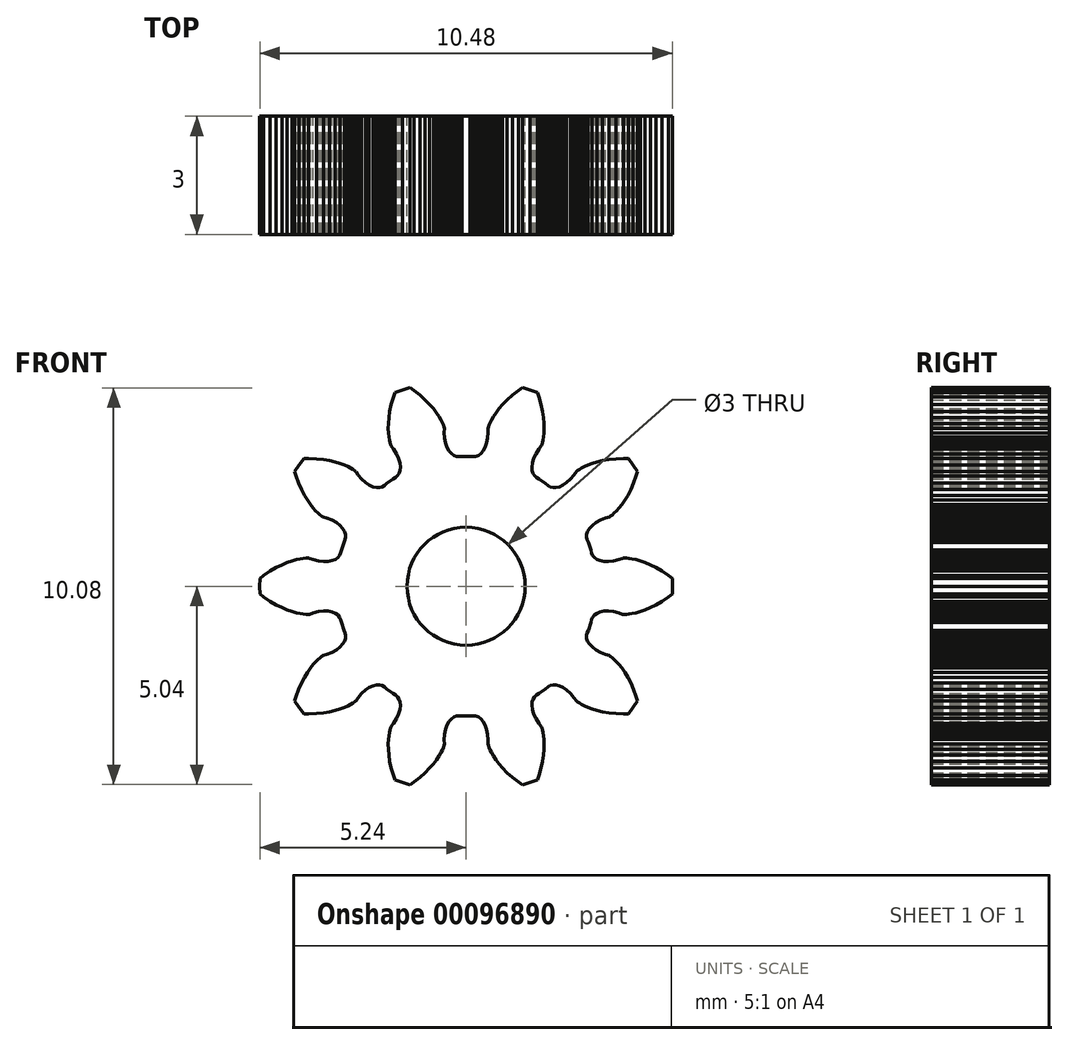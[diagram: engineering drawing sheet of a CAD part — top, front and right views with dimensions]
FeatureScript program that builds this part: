
annotation { "Feature Type Name" : "Feature", "Feature Type Description" : "" }
export const myFeature = defineFeature(function(context is Context, id is Id, definition is map)
    precondition{}
    {
        {
            var Q0;
            Q0=qCreatedBy(makeId("Front.planeOp"),FACE);
            var sketch = newSketch(context, id + "F0", { "sketchPlane" : qUnion([Q0])});
            skCircle(sketch, "E0", {"center": v(0, 0) * mm, "radius": 1.5 * mm});
            skSolve(sketch);
        }
        {
            var Q0;
            Q0=qCreatedBy(makeId("Front.planeOp"),FACE);
            var sketch = newSketch(context, id + "F1", { "sketchPlane" : qUnion([Q0])});
            skLineSegment(sketch, "E1", {"start": v(4.12, -3.24) * mm, "end": v(4.24, -3.08) * mm});
            skLineSegment(sketch, "E2", {"start": v(4.24, -3.08) * mm, "end": v(4.36, -2.92) * mm});
            skLineSegment(sketch, "E3", {"start": v(4.36, -2.92) * mm, "end": v(4.32, -2.8) * mm});
            skLineSegment(sketch, "E4", {"start": v(4.32, -2.8) * mm, "end": v(4.25, -2.62) * mm});
            skLineSegment(sketch, "E5", {"start": v(4.25, -2.62) * mm, "end": v(4.18, -2.46) * mm});
            skLineSegment(sketch, "E6", {"start": v(4.18, -2.46) * mm, "end": v(4.1, -2.31) * mm});
            skLineSegment(sketch, "E7", {"start": v(4.1, -2.31) * mm, "end": v(4.03, -2.19) * mm});
            skLineSegment(sketch, "E8", {"start": v(4.03, -2.19) * mm, "end": v(3.96, -2.08) * mm});
            skLineSegment(sketch, "E9", {"start": v(3.96, -2.08) * mm, "end": v(3.89, -2) * mm});
            skLineSegment(sketch, "E10", {"start": v(3.89, -2) * mm, "end": v(3.82, -1.92) * mm});
            skLineSegment(sketch, "E11", {"start": v(3.82, -1.92) * mm, "end": v(3.76, -1.86) * mm});
            skLineSegment(sketch, "E12", {"start": v(3.76, -1.86) * mm, "end": v(3.71, -1.82) * mm});
            skLineSegment(sketch, "E13", {"start": v(3.71, -1.82) * mm, "end": v(3.67, -1.79) * mm});
            skLineSegment(sketch, "E14", {"start": v(3.67, -1.79) * mm, "end": v(3.64, -1.77) * mm});
            skLineSegment(sketch, "E15", {"start": v(3.64, -1.77) * mm, "end": v(3.64, -1.76) * mm});
            skLineSegment(sketch, "E16", {"start": v(3.64, -1.76) * mm, "end": v(3.54, -1.74) * mm});
            skLineSegment(sketch, "E17", {"start": v(3.54, -1.74) * mm, "end": v(3.4, -1.68) * mm});
            skLineSegment(sketch, "E18", {"start": v(3.4, -1.68) * mm, "end": v(3.3, -1.62) * mm});
            skLineSegment(sketch, "E19", {"start": v(3.3, -1.62) * mm, "end": v(3.2, -1.55) * mm});
            skLineSegment(sketch, "E20", {"start": v(3.2, -1.55) * mm, "end": v(3.14, -1.47) * mm});
            skLineSegment(sketch, "E21", {"start": v(3.14, -1.47) * mm, "end": v(3.09, -1.4) * mm});
            skLineSegment(sketch, "E22", {"start": v(3.09, -1.4) * mm, "end": v(3.06, -1.32) * mm});
            skLineSegment(sketch, "E23", {"start": v(3.06, -1.32) * mm, "end": v(3.06, -1.25) * mm});
            skLineSegment(sketch, "E24", {"start": v(3.06, -1.25) * mm, "end": v(3.08, -1.18) * mm});
            skLineSegment(sketch, "E25", {"start": v(3.08, -1.18) * mm, "end": v(3.1, -1.12) * mm});
            skLineSegment(sketch, "E26", {"start": v(3.1, -1.12) * mm, "end": v(3.17, -0.92) * mm});
            skLineSegment(sketch, "E27", {"start": v(3.17, -0.92) * mm, "end": v(3.18, -0.85) * mm});
            skLineSegment(sketch, "E28", {"start": v(3.18, -0.85) * mm, "end": v(3.2, -0.79) * mm});
            skLineSegment(sketch, "E29", {"start": v(3.2, -0.79) * mm, "end": v(3.26, -0.73) * mm});
            skLineSegment(sketch, "E30", {"start": v(3.26, -0.73) * mm, "end": v(3.32, -0.69) * mm});
            skLineSegment(sketch, "E31", {"start": v(3.32, -0.69) * mm, "end": v(3.4, -0.65) * mm});
            skLineSegment(sketch, "E32", {"start": v(3.4, -0.65) * mm, "end": v(3.5, -0.63) * mm});
            skLineSegment(sketch, "E33", {"start": v(3.5, -0.63) * mm, "end": v(3.62, -0.63) * mm});
            skLineSegment(sketch, "E34", {"start": v(3.62, -0.63) * mm, "end": v(3.75, -0.64) * mm});
            skLineSegment(sketch, "E35", {"start": v(3.75, -0.64) * mm, "end": v(3.89, -0.68) * mm});
            skLineSegment(sketch, "E36", {"start": v(3.89, -0.68) * mm, "end": v(3.98, -0.71) * mm});
            skLineSegment(sketch, "E37", {"start": v(3.98, -0.71) * mm, "end": v(3.99, -0.71) * mm});
            skLineSegment(sketch, "E38", {"start": v(3.99, -0.71) * mm, "end": v(4.02, -0.71) * mm});
            skLineSegment(sketch, "E39", {"start": v(4.02, -0.71) * mm, "end": v(4.07, -0.71) * mm});
            skLineSegment(sketch, "E40", {"start": v(4.07, -0.71) * mm, "end": v(4.14, -0.7) * mm});
            skLineSegment(sketch, "E41", {"start": v(4.14, -0.7) * mm, "end": v(4.22, -0.7) * mm});
            skLineSegment(sketch, "E42", {"start": v(4.22, -0.7) * mm, "end": v(4.31, -0.67) * mm});
            skLineSegment(sketch, "E43", {"start": v(4.31, -0.67) * mm, "end": v(4.42, -0.64) * mm});
            skLineSegment(sketch, "E44", {"start": v(4.42, -0.64) * mm, "end": v(4.55, -0.6) * mm});
            skLineSegment(sketch, "E45", {"start": v(4.55, -0.6) * mm, "end": v(4.68, -0.54) * mm});
            skLineSegment(sketch, "E46", {"start": v(4.68, -0.54) * mm, "end": v(4.83, -0.47) * mm});
            skLineSegment(sketch, "E47", {"start": v(4.83, -0.47) * mm, "end": v(4.98, -0.38) * mm});
            skLineSegment(sketch, "E48", {"start": v(4.98, -0.38) * mm, "end": v(5.14, -0.27) * mm});
            skLineSegment(sketch, "E49", {"start": v(5.14, -0.27) * mm, "end": v(5.24, -0.2) * mm});
            skLineSegment(sketch, "E50", {"start": v(5.24, -0.2) * mm, "end": v(5.24, 0) * mm});
            skLineSegment(sketch, "E51", {"start": v(5.24, 0) * mm, "end": v(5.24, 0.2) * mm});
            skLineSegment(sketch, "E52", {"start": v(5.24, 0.2) * mm, "end": v(5.14, 0.27) * mm});
            skLineSegment(sketch, "E53", {"start": v(5.14, 0.27) * mm, "end": v(4.98, 0.38) * mm});
            skLineSegment(sketch, "E54", {"start": v(4.98, 0.38) * mm, "end": v(4.83, 0.47) * mm});
            skLineSegment(sketch, "E55", {"start": v(4.83, 0.47) * mm, "end": v(4.68, 0.54) * mm});
            skLineSegment(sketch, "E56", {"start": v(4.68, 0.54) * mm, "end": v(4.55, 0.6) * mm});
            skLineSegment(sketch, "E57", {"start": v(4.55, 0.6) * mm, "end": v(4.42, 0.64) * mm});
            skLineSegment(sketch, "E58", {"start": v(4.42, 0.64) * mm, "end": v(4.31, 0.67) * mm});
            skLineSegment(sketch, "E59", {"start": v(4.31, 0.67) * mm, "end": v(4.22, 0.7) * mm});
            skLineSegment(sketch, "E60", {"start": v(4.22, 0.7) * mm, "end": v(4.14, 0.7) * mm});
            skLineSegment(sketch, "E61", {"start": v(4.14, 0.7) * mm, "end": v(4.07, 0.71) * mm});
            skLineSegment(sketch, "E62", {"start": v(4.07, 0.71) * mm, "end": v(4.02, 0.71) * mm});
            skLineSegment(sketch, "E63", {"start": v(4.02, 0.71) * mm, "end": v(3.99, 0.71) * mm});
            skLineSegment(sketch, "E64", {"start": v(3.99, 0.71) * mm, "end": v(3.98, 0.71) * mm});
            skLineSegment(sketch, "E65", {"start": v(3.98, 0.71) * mm, "end": v(3.89, 0.68) * mm});
            skLineSegment(sketch, "E66", {"start": v(3.89, 0.68) * mm, "end": v(3.75, 0.64) * mm});
            skLineSegment(sketch, "E67", {"start": v(3.75, 0.64) * mm, "end": v(3.62, 0.63) * mm});
            skLineSegment(sketch, "E68", {"start": v(3.62, 0.63) * mm, "end": v(3.5, 0.63) * mm});
            skLineSegment(sketch, "E69", {"start": v(3.5, 0.63) * mm, "end": v(3.4, 0.65) * mm});
            skLineSegment(sketch, "E70", {"start": v(3.4, 0.65) * mm, "end": v(3.32, 0.69) * mm});
            skLineSegment(sketch, "E71", {"start": v(3.32, 0.69) * mm, "end": v(3.26, 0.73) * mm});
            skLineSegment(sketch, "E72", {"start": v(3.26, 0.73) * mm, "end": v(3.2, 0.79) * mm});
            skLineSegment(sketch, "E73", {"start": v(3.2, 0.79) * mm, "end": v(3.18, 0.85) * mm});
            skLineSegment(sketch, "E74", {"start": v(3.18, 0.85) * mm, "end": v(3.17, 0.92) * mm});
            skLineSegment(sketch, "E75", {"start": v(3.17, 0.92) * mm, "end": v(3.1, 1.12) * mm});
            skLineSegment(sketch, "E76", {"start": v(3.1, 1.12) * mm, "end": v(3.08, 1.18) * mm});
            skLineSegment(sketch, "E77", {"start": v(3.08, 1.18) * mm, "end": v(3.06, 1.25) * mm});
            skLineSegment(sketch, "E78", {"start": v(3.06, 1.25) * mm, "end": v(3.06, 1.32) * mm});
            skLineSegment(sketch, "E79", {"start": v(3.06, 1.32) * mm, "end": v(3.09, 1.4) * mm});
            skLineSegment(sketch, "E80", {"start": v(3.09, 1.4) * mm, "end": v(3.14, 1.47) * mm});
            skLineSegment(sketch, "E81", {"start": v(3.14, 1.47) * mm, "end": v(3.2, 1.55) * mm});
            skLineSegment(sketch, "E82", {"start": v(3.2, 1.55) * mm, "end": v(3.3, 1.62) * mm});
            skLineSegment(sketch, "E83", {"start": v(3.3, 1.62) * mm, "end": v(3.4, 1.68) * mm});
            skLineSegment(sketch, "E84", {"start": v(3.4, 1.68) * mm, "end": v(3.54, 1.74) * mm});
            skLineSegment(sketch, "E85", {"start": v(3.54, 1.74) * mm, "end": v(3.64, 1.76) * mm});
            skLineSegment(sketch, "E86", {"start": v(3.64, 1.76) * mm, "end": v(3.64, 1.77) * mm});
            skLineSegment(sketch, "E87", {"start": v(3.64, 1.77) * mm, "end": v(3.67, 1.79) * mm});
            skLineSegment(sketch, "E88", {"start": v(3.67, 1.79) * mm, "end": v(3.71, 1.82) * mm});
            skLineSegment(sketch, "E89", {"start": v(3.71, 1.82) * mm, "end": v(3.76, 1.86) * mm});
            skLineSegment(sketch, "E90", {"start": v(3.76, 1.86) * mm, "end": v(3.82, 1.92) * mm});
            skLineSegment(sketch, "E91", {"start": v(3.82, 1.92) * mm, "end": v(3.89, 2) * mm});
            skLineSegment(sketch, "E92", {"start": v(3.89, 2) * mm, "end": v(3.96, 2.08) * mm});
            skLineSegment(sketch, "E93", {"start": v(3.96, 2.08) * mm, "end": v(4.03, 2.19) * mm});
            skLineSegment(sketch, "E94", {"start": v(4.03, 2.19) * mm, "end": v(4.1, 2.31) * mm});
            skLineSegment(sketch, "E95", {"start": v(4.1, 2.31) * mm, "end": v(4.18, 2.46) * mm});
            skLineSegment(sketch, "E96", {"start": v(4.18, 2.46) * mm, "end": v(4.25, 2.62) * mm});
            skLineSegment(sketch, "E97", {"start": v(4.25, 2.62) * mm, "end": v(4.32, 2.8) * mm});
            skLineSegment(sketch, "E98", {"start": v(4.32, 2.8) * mm, "end": v(4.36, 2.92) * mm});
            skLineSegment(sketch, "E99", {"start": v(4.36, 2.92) * mm, "end": v(4.24, 3.08) * mm});
            skLineSegment(sketch, "E100", {"start": v(4.24, 3.08) * mm, "end": v(4.12, 3.24) * mm});
            skLineSegment(sketch, "E101", {"start": v(4.12, 3.24) * mm, "end": v(4, 3.24) * mm});
            skLineSegment(sketch, "E102", {"start": v(4, 3.24) * mm, "end": v(3.8, 3.24) * mm});
            skLineSegment(sketch, "E103", {"start": v(3.8, 3.24) * mm, "end": v(3.63, 3.22) * mm});
            skLineSegment(sketch, "E104", {"start": v(3.63, 3.22) * mm, "end": v(3.47, 3.2) * mm});
            skLineSegment(sketch, "E105", {"start": v(3.47, 3.2) * mm, "end": v(3.33, 3.16) * mm});
            skLineSegment(sketch, "E106", {"start": v(3.33, 3.16) * mm, "end": v(3.2, 3.12) * mm});
            skLineSegment(sketch, "E107", {"start": v(3.2, 3.12) * mm, "end": v(3.1, 3.08) * mm});
            skLineSegment(sketch, "E108", {"start": v(3.1, 3.08) * mm, "end": v(3, 3.04) * mm});
            skLineSegment(sketch, "E109", {"start": v(3, 3.04) * mm, "end": v(2.93, 3) * mm});
            skLineSegment(sketch, "E110", {"start": v(2.93, 3) * mm, "end": v(2.87, 2.97) * mm});
            skLineSegment(sketch, "E111", {"start": v(2.87, 2.97) * mm, "end": v(2.83, 2.94) * mm});
            skLineSegment(sketch, "E112", {"start": v(2.83, 2.94) * mm, "end": v(2.8, 2.92) * mm});
            skLineSegment(sketch, "E113", {"start": v(2.8, 2.92) * mm, "end": v(2.8, 2.91) * mm});
            skLineSegment(sketch, "E114", {"start": v(2.8, 2.91) * mm, "end": v(2.74, 2.83) * mm});
            skLineSegment(sketch, "E115", {"start": v(2.74, 2.83) * mm, "end": v(2.65, 2.72) * mm});
            skLineSegment(sketch, "E116", {"start": v(2.65, 2.72) * mm, "end": v(2.56, 2.64) * mm});
            skLineSegment(sketch, "E117", {"start": v(2.56, 2.64) * mm, "end": v(2.46, 2.57) * mm});
            skLineSegment(sketch, "E118", {"start": v(2.46, 2.57) * mm, "end": v(2.37, 2.53) * mm});
            skLineSegment(sketch, "E119", {"start": v(2.37, 2.53) * mm, "end": v(2.28, 2.5) * mm});
            skLineSegment(sketch, "E120", {"start": v(2.28, 2.5) * mm, "end": v(2.2, 2.5) * mm});
            skLineSegment(sketch, "E121", {"start": v(2.2, 2.5) * mm, "end": v(2.13, 2.52) * mm});
            skLineSegment(sketch, "E122", {"start": v(2.13, 2.52) * mm, "end": v(2.08, 2.56) * mm});
            skLineSegment(sketch, "E123", {"start": v(2.08, 2.56) * mm, "end": v(2.02, 2.6) * mm});
            skLineSegment(sketch, "E124", {"start": v(2.02, 2.6) * mm, "end": v(1.85, 2.73) * mm});
            skLineSegment(sketch, "E125", {"start": v(1.85, 2.73) * mm, "end": v(1.8, 2.77) * mm});
            skLineSegment(sketch, "E126", {"start": v(1.8, 2.77) * mm, "end": v(1.74, 2.8) * mm});
            skLineSegment(sketch, "E127", {"start": v(1.74, 2.8) * mm, "end": v(1.7, 2.87) * mm});
            skLineSegment(sketch, "E128", {"start": v(1.7, 2.87) * mm, "end": v(1.68, 2.95) * mm});
            skLineSegment(sketch, "E129", {"start": v(1.68, 2.95) * mm, "end": v(1.67, 3.03) * mm});
            skLineSegment(sketch, "E130", {"start": v(1.67, 3.03) * mm, "end": v(1.68, 3.13) * mm});
            skLineSegment(sketch, "E131", {"start": v(1.68, 3.13) * mm, "end": v(1.72, 3.25) * mm});
            skLineSegment(sketch, "E132", {"start": v(1.72, 3.25) * mm, "end": v(1.77, 3.36) * mm});
            skLineSegment(sketch, "E133", {"start": v(1.77, 3.36) * mm, "end": v(1.85, 3.49) * mm});
            skLineSegment(sketch, "E134", {"start": v(1.85, 3.49) * mm, "end": v(1.9, 3.56) * mm});
            skLineSegment(sketch, "E135", {"start": v(1.9, 3.56) * mm, "end": v(1.9, 3.57) * mm});
            skLineSegment(sketch, "E136", {"start": v(1.9, 3.57) * mm, "end": v(1.92, 3.6) * mm});
            skLineSegment(sketch, "E137", {"start": v(1.92, 3.6) * mm, "end": v(1.94, 3.65) * mm});
            skLineSegment(sketch, "E138", {"start": v(1.94, 3.65) * mm, "end": v(1.95, 3.72) * mm});
            skLineSegment(sketch, "E139", {"start": v(1.95, 3.72) * mm, "end": v(1.96, 3.8) * mm});
            skLineSegment(sketch, "E140", {"start": v(1.96, 3.8) * mm, "end": v(1.97, 3.9) * mm});
            skLineSegment(sketch, "E141", {"start": v(1.97, 3.9) * mm, "end": v(1.98, 4) * mm});
            skLineSegment(sketch, "E142", {"start": v(1.98, 4) * mm, "end": v(1.98, 4.14) * mm});
            skLineSegment(sketch, "E143", {"start": v(1.98, 4.14) * mm, "end": v(1.96, 4.28) * mm});
            skLineSegment(sketch, "E144", {"start": v(1.96, 4.28) * mm, "end": v(1.94, 4.44) * mm});
            skLineSegment(sketch, "E145", {"start": v(1.94, 4.44) * mm, "end": v(1.9, 4.62) * mm});
            skLineSegment(sketch, "E146", {"start": v(1.9, 4.62) * mm, "end": v(1.85, 4.8) * mm});
            skLineSegment(sketch, "E147", {"start": v(1.85, 4.8) * mm, "end": v(1.81, 4.92) * mm});
            skLineSegment(sketch, "E148", {"start": v(1.81, 4.92) * mm, "end": v(1.62, 4.99) * mm});
            skLineSegment(sketch, "E149", {"start": v(1.62, 4.99) * mm, "end": v(1.43, 5.04) * mm});
            skLineSegment(sketch, "E150", {"start": v(1.43, 5.04) * mm, "end": v(1.33, 4.97) * mm});
            skLineSegment(sketch, "E151", {"start": v(1.33, 4.97) * mm, "end": v(1.18, 4.85) * mm});
            skLineSegment(sketch, "E152", {"start": v(1.18, 4.85) * mm, "end": v(1.04, 4.74) * mm});
            skLineSegment(sketch, "E153", {"start": v(1.04, 4.74) * mm, "end": v(0.93, 4.62) * mm});
            skLineSegment(sketch, "E154", {"start": v(0.93, 4.62) * mm, "end": v(0.83, 4.51) * mm});
            skLineSegment(sketch, "E155", {"start": v(0.83, 4.51) * mm, "end": v(0.76, 4.4) * mm});
            skLineSegment(sketch, "E156", {"start": v(0.76, 4.4) * mm, "end": v(0.7, 4.31) * mm});
            skLineSegment(sketch, "E157", {"start": v(0.7, 4.31) * mm, "end": v(0.64, 4.23) * mm});
            skLineSegment(sketch, "E158", {"start": v(0.64, 4.23) * mm, "end": v(0.6, 4.15) * mm});
            skLineSegment(sketch, "E159", {"start": v(0.6, 4.15) * mm, "end": v(0.58, 4.1) * mm});
            skLineSegment(sketch, "E160", {"start": v(0.58, 4.1) * mm, "end": v(0.56, 4.04) * mm});
            skLineSegment(sketch, "E161", {"start": v(0.56, 4.04) * mm, "end": v(0.55, 4.01) * mm});
            skLineSegment(sketch, "E162", {"start": v(0.55, 4.01) * mm, "end": v(0.55, 4) * mm});
            skLineSegment(sketch, "E163", {"start": v(0.55, 4) * mm, "end": v(0.56, 3.9) * mm});
            skLineSegment(sketch, "E164", {"start": v(0.56, 3.9) * mm, "end": v(0.54, 3.76) * mm});
            skLineSegment(sketch, "E165", {"start": v(0.54, 3.76) * mm, "end": v(0.52, 3.63) * mm});
            skLineSegment(sketch, "E166", {"start": v(0.52, 3.63) * mm, "end": v(0.48, 3.53) * mm});
            skLineSegment(sketch, "E167", {"start": v(0.48, 3.53) * mm, "end": v(0.43, 3.44) * mm});
            skLineSegment(sketch, "E168", {"start": v(0.43, 3.44) * mm, "end": v(0.37, 3.37) * mm});
            skLineSegment(sketch, "E169", {"start": v(0.37, 3.37) * mm, "end": v(0.31, 3.32) * mm});
            skLineSegment(sketch, "E170", {"start": v(0.31, 3.32) * mm, "end": v(0.24, 3.3) * mm});
            skLineSegment(sketch, "E171", {"start": v(0.24, 3.3) * mm, "end": v(0.18, 3.3) * mm});
            skLineSegment(sketch, "E172", {"start": v(0.18, 3.3) * mm, "end": v(0.1, 3.3) * mm});
            skLineSegment(sketch, "E173", {"start": v(0.1, 3.3) * mm, "end": v(-0.1, 3.3) * mm});
            skLineSegment(sketch, "E174", {"start": v(-0.1, 3.3) * mm, "end": v(-0.18, 3.3) * mm});
            skLineSegment(sketch, "E175", {"start": v(-0.18, 3.3) * mm, "end": v(-0.24, 3.3) * mm});
            skLineSegment(sketch, "E176", {"start": v(-0.24, 3.3) * mm, "end": v(-0.31, 3.32) * mm});
            skLineSegment(sketch, "E177", {"start": v(-0.31, 3.32) * mm, "end": v(-0.37, 3.37) * mm});
            skLineSegment(sketch, "E178", {"start": v(-0.37, 3.37) * mm, "end": v(-0.43, 3.44) * mm});
            skLineSegment(sketch, "E179", {"start": v(-0.43, 3.44) * mm, "end": v(-0.48, 3.53) * mm});
            skLineSegment(sketch, "E180", {"start": v(-0.48, 3.53) * mm, "end": v(-0.52, 3.63) * mm});
            skLineSegment(sketch, "E181", {"start": v(-0.52, 3.63) * mm, "end": v(-0.54, 3.76) * mm});
            skLineSegment(sketch, "E182", {"start": v(-0.54, 3.76) * mm, "end": v(-0.56, 3.9) * mm});
            skLineSegment(sketch, "E183", {"start": v(-0.56, 3.9) * mm, "end": v(-0.55, 4) * mm});
            skLineSegment(sketch, "E184", {"start": v(-0.55, 4) * mm, "end": v(-0.55, 4.01) * mm});
            skLineSegment(sketch, "E185", {"start": v(-0.55, 4.01) * mm, "end": v(-0.56, 4.04) * mm});
            skLineSegment(sketch, "E186", {"start": v(-0.56, 4.04) * mm, "end": v(-0.58, 4.1) * mm});
            skLineSegment(sketch, "E187", {"start": v(-0.58, 4.1) * mm, "end": v(-0.6, 4.15) * mm});
            skLineSegment(sketch, "E188", {"start": v(-0.6, 4.15) * mm, "end": v(-0.64, 4.23) * mm});
            skLineSegment(sketch, "E189", {"start": v(-0.64, 4.23) * mm, "end": v(-0.7, 4.31) * mm});
            skLineSegment(sketch, "E190", {"start": v(-0.7, 4.31) * mm, "end": v(-0.76, 4.4) * mm});
            skLineSegment(sketch, "E191", {"start": v(-0.76, 4.4) * mm, "end": v(-0.83, 4.51) * mm});
            skLineSegment(sketch, "E192", {"start": v(-0.83, 4.51) * mm, "end": v(-0.93, 4.62) * mm});
            skLineSegment(sketch, "E193", {"start": v(-0.93, 4.62) * mm, "end": v(-1.04, 4.74) * mm});
            skLineSegment(sketch, "E194", {"start": v(-1.04, 4.74) * mm, "end": v(-1.18, 4.85) * mm});
            skLineSegment(sketch, "E195", {"start": v(-1.18, 4.85) * mm, "end": v(-1.33, 4.97) * mm});
            skLineSegment(sketch, "E196", {"start": v(-1.33, 4.97) * mm, "end": v(-1.43, 5.04) * mm});
            skLineSegment(sketch, "E197", {"start": v(-1.43, 5.04) * mm, "end": v(-1.62, 4.99) * mm});
            skLineSegment(sketch, "E198", {"start": v(-1.62, 4.99) * mm, "end": v(-1.81, 4.92) * mm});
            skLineSegment(sketch, "E199", {"start": v(-1.81, 4.92) * mm, "end": v(-1.85, 4.8) * mm});
            skLineSegment(sketch, "E200", {"start": v(-1.85, 4.8) * mm, "end": v(-1.9, 4.62) * mm});
            skLineSegment(sketch, "E201", {"start": v(-1.9, 4.62) * mm, "end": v(-1.94, 4.44) * mm});
            skLineSegment(sketch, "E202", {"start": v(-1.94, 4.44) * mm, "end": v(-1.96, 4.28) * mm});
            skLineSegment(sketch, "E203", {"start": v(-1.96, 4.28) * mm, "end": v(-1.98, 4.14) * mm});
            skLineSegment(sketch, "E204", {"start": v(-1.98, 4.14) * mm, "end": v(-1.98, 4) * mm});
            skLineSegment(sketch, "E205", {"start": v(-1.98, 4) * mm, "end": v(-1.97, 3.9) * mm});
            skLineSegment(sketch, "E206", {"start": v(-1.97, 3.9) * mm, "end": v(-1.96, 3.8) * mm});
            skLineSegment(sketch, "E207", {"start": v(-1.96, 3.8) * mm, "end": v(-1.95, 3.72) * mm});
            skLineSegment(sketch, "E208", {"start": v(-1.95, 3.72) * mm, "end": v(-1.94, 3.65) * mm});
            skLineSegment(sketch, "E209", {"start": v(-1.94, 3.65) * mm, "end": v(-1.92, 3.6) * mm});
            skLineSegment(sketch, "E210", {"start": v(-1.92, 3.6) * mm, "end": v(-1.9, 3.57) * mm});
            skLineSegment(sketch, "E211", {"start": v(-1.9, 3.57) * mm, "end": v(-1.9, 3.56) * mm});
            skLineSegment(sketch, "E212", {"start": v(-1.9, 3.56) * mm, "end": v(-1.85, 3.49) * mm});
            skLineSegment(sketch, "E213", {"start": v(-1.85, 3.49) * mm, "end": v(-1.77, 3.36) * mm});
            skLineSegment(sketch, "E214", {"start": v(-1.77, 3.36) * mm, "end": v(-1.72, 3.25) * mm});
            skLineSegment(sketch, "E215", {"start": v(-1.72, 3.25) * mm, "end": v(-1.68, 3.13) * mm});
            skLineSegment(sketch, "E216", {"start": v(-1.68, 3.13) * mm, "end": v(-1.67, 3.03) * mm});
            skLineSegment(sketch, "E217", {"start": v(-1.67, 3.03) * mm, "end": v(-1.68, 2.95) * mm});
            skLineSegment(sketch, "E218", {"start": v(-1.68, 2.95) * mm, "end": v(-1.7, 2.87) * mm});
            skLineSegment(sketch, "E219", {"start": v(-1.7, 2.87) * mm, "end": v(-1.74, 2.8) * mm});
            skLineSegment(sketch, "E220", {"start": v(-1.74, 2.8) * mm, "end": v(-1.8, 2.77) * mm});
            skLineSegment(sketch, "E221", {"start": v(-1.8, 2.77) * mm, "end": v(-1.85, 2.73) * mm});
            skLineSegment(sketch, "E222", {"start": v(-1.85, 2.73) * mm, "end": v(-2.02, 2.6) * mm});
            skLineSegment(sketch, "E223", {"start": v(-2.02, 2.6) * mm, "end": v(-2.08, 2.56) * mm});
            skLineSegment(sketch, "E224", {"start": v(-2.08, 2.56) * mm, "end": v(-2.13, 2.52) * mm});
            skLineSegment(sketch, "E225", {"start": v(-2.13, 2.52) * mm, "end": v(-2.2, 2.5) * mm});
            skLineSegment(sketch, "E226", {"start": v(-2.2, 2.5) * mm, "end": v(-2.28, 2.5) * mm});
            skLineSegment(sketch, "E227", {"start": v(-2.28, 2.5) * mm, "end": v(-2.37, 2.53) * mm});
            skLineSegment(sketch, "E228", {"start": v(-2.37, 2.53) * mm, "end": v(-2.46, 2.57) * mm});
            skLineSegment(sketch, "E229", {"start": v(-2.46, 2.57) * mm, "end": v(-2.56, 2.64) * mm});
            skLineSegment(sketch, "E230", {"start": v(-2.56, 2.64) * mm, "end": v(-2.65, 2.72) * mm});
            skLineSegment(sketch, "E231", {"start": v(-2.65, 2.72) * mm, "end": v(-2.74, 2.83) * mm});
            skLineSegment(sketch, "E232", {"start": v(-2.74, 2.83) * mm, "end": v(-2.8, 2.91) * mm});
            skLineSegment(sketch, "E233", {"start": v(-2.8, 2.91) * mm, "end": v(-2.8, 2.92) * mm});
            skLineSegment(sketch, "E234", {"start": v(-2.8, 2.92) * mm, "end": v(-2.83, 2.94) * mm});
            skLineSegment(sketch, "E235", {"start": v(-2.83, 2.94) * mm, "end": v(-2.87, 2.97) * mm});
            skLineSegment(sketch, "E236", {"start": v(-2.87, 2.97) * mm, "end": v(-2.93, 3) * mm});
            skLineSegment(sketch, "E237", {"start": v(-2.93, 3) * mm, "end": v(-3, 3.04) * mm});
            skLineSegment(sketch, "E238", {"start": v(-3, 3.04) * mm, "end": v(-3.1, 3.08) * mm});
            skLineSegment(sketch, "E239", {"start": v(-3.1, 3.08) * mm, "end": v(-3.2, 3.12) * mm});
            skLineSegment(sketch, "E240", {"start": v(-3.2, 3.12) * mm, "end": v(-3.33, 3.16) * mm});
            skLineSegment(sketch, "E241", {"start": v(-3.33, 3.16) * mm, "end": v(-3.47, 3.2) * mm});
            skLineSegment(sketch, "E242", {"start": v(-3.47, 3.2) * mm, "end": v(-3.63, 3.22) * mm});
            skLineSegment(sketch, "E243", {"start": v(-3.63, 3.22) * mm, "end": v(-3.8, 3.24) * mm});
            skLineSegment(sketch, "E244", {"start": v(-3.8, 3.24) * mm, "end": v(-4, 3.24) * mm});
            skLineSegment(sketch, "E245", {"start": v(-4, 3.24) * mm, "end": v(-4.12, 3.24) * mm});
            skLineSegment(sketch, "E246", {"start": v(-4.12, 3.24) * mm, "end": v(-4.24, 3.08) * mm});
            skLineSegment(sketch, "E247", {"start": v(-4.24, 3.08) * mm, "end": v(-4.36, 2.92) * mm});
            skLineSegment(sketch, "E248", {"start": v(-4.36, 2.92) * mm, "end": v(-4.32, 2.8) * mm});
            skLineSegment(sketch, "E249", {"start": v(-4.32, 2.8) * mm, "end": v(-4.25, 2.62) * mm});
            skLineSegment(sketch, "E250", {"start": v(-4.25, 2.62) * mm, "end": v(-4.18, 2.46) * mm});
            skLineSegment(sketch, "E251", {"start": v(-4.18, 2.46) * mm, "end": v(-4.1, 2.31) * mm});
            skLineSegment(sketch, "E252", {"start": v(-4.1, 2.31) * mm, "end": v(-4.03, 2.19) * mm});
            skLineSegment(sketch, "E253", {"start": v(-4.03, 2.19) * mm, "end": v(-3.96, 2.08) * mm});
            skLineSegment(sketch, "E254", {"start": v(-3.96, 2.08) * mm, "end": v(-3.89, 2) * mm});
            skLineSegment(sketch, "E255", {"start": v(-3.89, 2) * mm, "end": v(-3.82, 1.92) * mm});
            skLineSegment(sketch, "E256", {"start": v(-3.82, 1.92) * mm, "end": v(-3.76, 1.86) * mm});
            skLineSegment(sketch, "E257", {"start": v(-3.76, 1.86) * mm, "end": v(-3.71, 1.82) * mm});
            skLineSegment(sketch, "E258", {"start": v(-3.71, 1.82) * mm, "end": v(-3.67, 1.79) * mm});
            skLineSegment(sketch, "E259", {"start": v(-3.67, 1.79) * mm, "end": v(-3.64, 1.77) * mm});
            skLineSegment(sketch, "E260", {"start": v(-3.64, 1.77) * mm, "end": v(-3.64, 1.76) * mm});
            skLineSegment(sketch, "E261", {"start": v(-3.64, 1.76) * mm, "end": v(-3.54, 1.74) * mm});
            skLineSegment(sketch, "E262", {"start": v(-3.54, 1.74) * mm, "end": v(-3.4, 1.68) * mm});
            skLineSegment(sketch, "E263", {"start": v(-3.4, 1.68) * mm, "end": v(-3.3, 1.62) * mm});
            skLineSegment(sketch, "E264", {"start": v(-3.3, 1.62) * mm, "end": v(-3.2, 1.55) * mm});
            skLineSegment(sketch, "E265", {"start": v(-3.2, 1.55) * mm, "end": v(-3.14, 1.47) * mm});
            skLineSegment(sketch, "E266", {"start": v(-3.14, 1.47) * mm, "end": v(-3.09, 1.4) * mm});
            skLineSegment(sketch, "E267", {"start": v(-3.09, 1.4) * mm, "end": v(-3.06, 1.32) * mm});
            skLineSegment(sketch, "E268", {"start": v(-3.06, 1.32) * mm, "end": v(-3.06, 1.25) * mm});
            skLineSegment(sketch, "E269", {"start": v(-3.06, 1.25) * mm, "end": v(-3.08, 1.18) * mm});
            skLineSegment(sketch, "E270", {"start": v(-3.08, 1.18) * mm, "end": v(-3.1, 1.12) * mm});
            skLineSegment(sketch, "E271", {"start": v(-3.1, 1.12) * mm, "end": v(-3.17, 0.92) * mm});
            skLineSegment(sketch, "E272", {"start": v(-3.17, 0.92) * mm, "end": v(-3.18, 0.85) * mm});
            skLineSegment(sketch, "E273", {"start": v(-3.18, 0.85) * mm, "end": v(-3.2, 0.79) * mm});
            skLineSegment(sketch, "E274", {"start": v(-3.2, 0.79) * mm, "end": v(-3.26, 0.73) * mm});
            skLineSegment(sketch, "E275", {"start": v(-3.26, 0.73) * mm, "end": v(-3.32, 0.69) * mm});
            skLineSegment(sketch, "E276", {"start": v(-3.32, 0.69) * mm, "end": v(-3.4, 0.65) * mm});
            skLineSegment(sketch, "E277", {"start": v(-3.4, 0.65) * mm, "end": v(-3.5, 0.63) * mm});
            skLineSegment(sketch, "E278", {"start": v(-3.5, 0.63) * mm, "end": v(-3.62, 0.63) * mm});
            skLineSegment(sketch, "E279", {"start": v(-3.62, 0.63) * mm, "end": v(-3.75, 0.64) * mm});
            skLineSegment(sketch, "E280", {"start": v(-3.75, 0.64) * mm, "end": v(-3.89, 0.68) * mm});
            skLineSegment(sketch, "E281", {"start": v(-3.89, 0.68) * mm, "end": v(-3.98, 0.71) * mm});
            skLineSegment(sketch, "E282", {"start": v(-3.98, 0.71) * mm, "end": v(-3.99, 0.71) * mm});
            skLineSegment(sketch, "E283", {"start": v(-3.99, 0.71) * mm, "end": v(-4.02, 0.71) * mm});
            skLineSegment(sketch, "E284", {"start": v(-4.02, 0.71) * mm, "end": v(-4.07, 0.71) * mm});
            skLineSegment(sketch, "E285", {"start": v(-4.07, 0.71) * mm, "end": v(-4.14, 0.7) * mm});
            skLineSegment(sketch, "E286", {"start": v(-4.14, 0.7) * mm, "end": v(-4.22, 0.7) * mm});
            skLineSegment(sketch, "E287", {"start": v(-4.22, 0.7) * mm, "end": v(-4.31, 0.67) * mm});
            skLineSegment(sketch, "E288", {"start": v(-4.31, 0.67) * mm, "end": v(-4.42, 0.64) * mm});
            skLineSegment(sketch, "E289", {"start": v(-4.42, 0.64) * mm, "end": v(-4.55, 0.6) * mm});
            skLineSegment(sketch, "E290", {"start": v(-4.55, 0.6) * mm, "end": v(-4.68, 0.54) * mm});
            skLineSegment(sketch, "E291", {"start": v(-4.68, 0.54) * mm, "end": v(-4.83, 0.47) * mm});
            skLineSegment(sketch, "E292", {"start": v(-4.83, 0.47) * mm, "end": v(-4.98, 0.38) * mm});
            skLineSegment(sketch, "E293", {"start": v(-4.98, 0.38) * mm, "end": v(-5.14, 0.27) * mm});
            skLineSegment(sketch, "E294", {"start": v(-5.14, 0.27) * mm, "end": v(-5.24, 0.2) * mm});
            skLineSegment(sketch, "E295", {"start": v(-5.24, 0.2) * mm, "end": v(-5.24, 0) * mm});
            skLineSegment(sketch, "E296", {"start": v(-5.24, 0) * mm, "end": v(-5.24, -0.2) * mm});
            skLineSegment(sketch, "E297", {"start": v(-5.24, -0.2) * mm, "end": v(-5.14, -0.27) * mm});
            skLineSegment(sketch, "E298", {"start": v(-5.14, -0.27) * mm, "end": v(-4.98, -0.38) * mm});
            skLineSegment(sketch, "E299", {"start": v(-4.98, -0.38) * mm, "end": v(-4.83, -0.47) * mm});
            skLineSegment(sketch, "E300", {"start": v(-4.83, -0.47) * mm, "end": v(-4.68, -0.54) * mm});
            skLineSegment(sketch, "E301", {"start": v(-4.68, -0.54) * mm, "end": v(-4.55, -0.6) * mm});
            skLineSegment(sketch, "E302", {"start": v(-4.55, -0.6) * mm, "end": v(-4.42, -0.64) * mm});
            skLineSegment(sketch, "E303", {"start": v(-4.42, -0.64) * mm, "end": v(-4.31, -0.67) * mm});
            skLineSegment(sketch, "E304", {"start": v(-4.31, -0.67) * mm, "end": v(-4.22, -0.7) * mm});
            skLineSegment(sketch, "E305", {"start": v(-4.22, -0.7) * mm, "end": v(-4.14, -0.7) * mm});
            skLineSegment(sketch, "E306", {"start": v(-4.14, -0.7) * mm, "end": v(-4.07, -0.71) * mm});
            skLineSegment(sketch, "E307", {"start": v(-4.07, -0.71) * mm, "end": v(-4.02, -0.71) * mm});
            skLineSegment(sketch, "E308", {"start": v(-4.02, -0.71) * mm, "end": v(-3.99, -0.71) * mm});
            skLineSegment(sketch, "E309", {"start": v(-3.99, -0.71) * mm, "end": v(-3.98, -0.71) * mm});
            skLineSegment(sketch, "E310", {"start": v(-3.98, -0.71) * mm, "end": v(-3.89, -0.68) * mm});
            skLineSegment(sketch, "E311", {"start": v(-3.89, -0.68) * mm, "end": v(-3.75, -0.64) * mm});
            skLineSegment(sketch, "E312", {"start": v(-3.75, -0.64) * mm, "end": v(-3.62, -0.63) * mm});
            skLineSegment(sketch, "E313", {"start": v(-3.62, -0.63) * mm, "end": v(-3.5, -0.63) * mm});
            skLineSegment(sketch, "E314", {"start": v(-3.5, -0.63) * mm, "end": v(-3.4, -0.65) * mm});
            skLineSegment(sketch, "E315", {"start": v(-3.4, -0.65) * mm, "end": v(-3.32, -0.69) * mm});
            skLineSegment(sketch, "E316", {"start": v(-3.32, -0.69) * mm, "end": v(-3.26, -0.73) * mm});
            skLineSegment(sketch, "E317", {"start": v(-3.26, -0.73) * mm, "end": v(-3.2, -0.79) * mm});
            skLineSegment(sketch, "E318", {"start": v(-3.2, -0.79) * mm, "end": v(-3.18, -0.85) * mm});
            skLineSegment(sketch, "E319", {"start": v(-3.18, -0.85) * mm, "end": v(-3.17, -0.92) * mm});
            skLineSegment(sketch, "E320", {"start": v(-3.17, -0.92) * mm, "end": v(-3.1, -1.12) * mm});
            skLineSegment(sketch, "E321", {"start": v(-3.1, -1.12) * mm, "end": v(-3.08, -1.18) * mm});
            skLineSegment(sketch, "E322", {"start": v(-3.08, -1.18) * mm, "end": v(-3.06, -1.25) * mm});
            skLineSegment(sketch, "E323", {"start": v(-3.06, -1.25) * mm, "end": v(-3.06, -1.32) * mm});
            skLineSegment(sketch, "E324", {"start": v(-3.06, -1.32) * mm, "end": v(-3.09, -1.4) * mm});
            skLineSegment(sketch, "E325", {"start": v(-3.09, -1.4) * mm, "end": v(-3.14, -1.47) * mm});
            skLineSegment(sketch, "E326", {"start": v(-3.14, -1.47) * mm, "end": v(-3.2, -1.55) * mm});
            skLineSegment(sketch, "E327", {"start": v(-3.2, -1.55) * mm, "end": v(-3.3, -1.62) * mm});
            skLineSegment(sketch, "E328", {"start": v(-3.3, -1.62) * mm, "end": v(-3.4, -1.68) * mm});
            skLineSegment(sketch, "E329", {"start": v(-3.4, -1.68) * mm, "end": v(-3.54, -1.74) * mm});
            skLineSegment(sketch, "E330", {"start": v(-3.54, -1.74) * mm, "end": v(-3.64, -1.76) * mm});
            skLineSegment(sketch, "E331", {"start": v(-3.64, -1.76) * mm, "end": v(-3.64, -1.77) * mm});
            skLineSegment(sketch, "E332", {"start": v(-3.64, -1.77) * mm, "end": v(-3.67, -1.79) * mm});
            skLineSegment(sketch, "E333", {"start": v(-3.67, -1.79) * mm, "end": v(-3.71, -1.82) * mm});
            skLineSegment(sketch, "E334", {"start": v(-3.71, -1.82) * mm, "end": v(-3.76, -1.86) * mm});
            skLineSegment(sketch, "E335", {"start": v(-3.76, -1.86) * mm, "end": v(-3.82, -1.92) * mm});
            skLineSegment(sketch, "E336", {"start": v(-3.82, -1.92) * mm, "end": v(-3.89, -2) * mm});
            skLineSegment(sketch, "E337", {"start": v(-3.89, -2) * mm, "end": v(-3.96, -2.08) * mm});
            skLineSegment(sketch, "E338", {"start": v(-3.96, -2.08) * mm, "end": v(-4.03, -2.19) * mm});
            skLineSegment(sketch, "E339", {"start": v(-4.03, -2.19) * mm, "end": v(-4.1, -2.31) * mm});
            skLineSegment(sketch, "E340", {"start": v(-4.1, -2.31) * mm, "end": v(-4.18, -2.46) * mm});
            skLineSegment(sketch, "E341", {"start": v(-4.18, -2.46) * mm, "end": v(-4.25, -2.62) * mm});
            skLineSegment(sketch, "E342", {"start": v(-4.25, -2.62) * mm, "end": v(-4.32, -2.8) * mm});
            skLineSegment(sketch, "E343", {"start": v(-4.32, -2.8) * mm, "end": v(-4.36, -2.92) * mm});
            skLineSegment(sketch, "E344", {"start": v(-4.36, -2.92) * mm, "end": v(-4.24, -3.08) * mm});
            skLineSegment(sketch, "E345", {"start": v(-4.24, -3.08) * mm, "end": v(-4.12, -3.24) * mm});
            skLineSegment(sketch, "E346", {"start": v(-4.12, -3.24) * mm, "end": v(-4, -3.24) * mm});
            skLineSegment(sketch, "E347", {"start": v(-4, -3.24) * mm, "end": v(-3.8, -3.24) * mm});
            skLineSegment(sketch, "E348", {"start": v(-3.8, -3.24) * mm, "end": v(-3.63, -3.22) * mm});
            skLineSegment(sketch, "E349", {"start": v(-3.63, -3.22) * mm, "end": v(-3.47, -3.2) * mm});
            skLineSegment(sketch, "E350", {"start": v(-3.47, -3.2) * mm, "end": v(-3.33, -3.16) * mm});
            skLineSegment(sketch, "E351", {"start": v(-3.33, -3.16) * mm, "end": v(-3.2, -3.12) * mm});
            skLineSegment(sketch, "E352", {"start": v(-3.2, -3.12) * mm, "end": v(-3.1, -3.08) * mm});
            skLineSegment(sketch, "E353", {"start": v(-3.1, -3.08) * mm, "end": v(-3, -3.04) * mm});
            skLineSegment(sketch, "E354", {"start": v(-3, -3.04) * mm, "end": v(-2.93, -3) * mm});
            skLineSegment(sketch, "E355", {"start": v(-2.93, -3) * mm, "end": v(-2.87, -2.97) * mm});
            skLineSegment(sketch, "E356", {"start": v(-2.87, -2.97) * mm, "end": v(-2.83, -2.94) * mm});
            skLineSegment(sketch, "E357", {"start": v(-2.83, -2.94) * mm, "end": v(-2.8, -2.92) * mm});
            skLineSegment(sketch, "E358", {"start": v(-2.8, -2.92) * mm, "end": v(-2.8, -2.91) * mm});
            skLineSegment(sketch, "E359", {"start": v(-2.8, -2.91) * mm, "end": v(-2.74, -2.83) * mm});
            skLineSegment(sketch, "E360", {"start": v(-2.74, -2.83) * mm, "end": v(-2.65, -2.72) * mm});
            skLineSegment(sketch, "E361", {"start": v(-2.65, -2.72) * mm, "end": v(-2.56, -2.64) * mm});
            skLineSegment(sketch, "E362", {"start": v(-2.56, -2.64) * mm, "end": v(-2.46, -2.57) * mm});
            skLineSegment(sketch, "E363", {"start": v(-2.46, -2.57) * mm, "end": v(-2.37, -2.53) * mm});
            skLineSegment(sketch, "E364", {"start": v(-2.37, -2.53) * mm, "end": v(-2.28, -2.5) * mm});
            skLineSegment(sketch, "E365", {"start": v(-2.28, -2.5) * mm, "end": v(-2.2, -2.5) * mm});
            skLineSegment(sketch, "E366", {"start": v(-2.2, -2.5) * mm, "end": v(-2.13, -2.52) * mm});
            skLineSegment(sketch, "E367", {"start": v(-2.13, -2.52) * mm, "end": v(-2.08, -2.56) * mm});
            skLineSegment(sketch, "E368", {"start": v(-2.08, -2.56) * mm, "end": v(-2.02, -2.6) * mm});
            skLineSegment(sketch, "E369", {"start": v(-2.02, -2.6) * mm, "end": v(-1.85, -2.73) * mm});
            skLineSegment(sketch, "E370", {"start": v(-1.85, -2.73) * mm, "end": v(-1.8, -2.77) * mm});
            skLineSegment(sketch, "E371", {"start": v(-1.8, -2.77) * mm, "end": v(-1.74, -2.8) * mm});
            skLineSegment(sketch, "E372", {"start": v(-1.74, -2.8) * mm, "end": v(-1.7, -2.87) * mm});
            skLineSegment(sketch, "E373", {"start": v(-1.7, -2.87) * mm, "end": v(-1.68, -2.95) * mm});
            skLineSegment(sketch, "E374", {"start": v(-1.68, -2.95) * mm, "end": v(-1.67, -3.03) * mm});
            skLineSegment(sketch, "E375", {"start": v(-1.67, -3.03) * mm, "end": v(-1.68, -3.13) * mm});
            skLineSegment(sketch, "E376", {"start": v(-1.68, -3.13) * mm, "end": v(-1.72, -3.25) * mm});
            skLineSegment(sketch, "E377", {"start": v(-1.72, -3.25) * mm, "end": v(-1.77, -3.36) * mm});
            skLineSegment(sketch, "E378", {"start": v(-1.77, -3.36) * mm, "end": v(-1.85, -3.49) * mm});
            skLineSegment(sketch, "E379", {"start": v(-1.85, -3.49) * mm, "end": v(-1.9, -3.56) * mm});
            skLineSegment(sketch, "E380", {"start": v(-1.9, -3.56) * mm, "end": v(-1.9, -3.57) * mm});
            skLineSegment(sketch, "E381", {"start": v(-1.9, -3.57) * mm, "end": v(-1.92, -3.6) * mm});
            skLineSegment(sketch, "E382", {"start": v(-1.92, -3.6) * mm, "end": v(-1.94, -3.65) * mm});
            skLineSegment(sketch, "E383", {"start": v(-1.94, -3.65) * mm, "end": v(-1.95, -3.72) * mm});
            skLineSegment(sketch, "E384", {"start": v(-1.95, -3.72) * mm, "end": v(-1.96, -3.8) * mm});
            skLineSegment(sketch, "E385", {"start": v(-1.96, -3.8) * mm, "end": v(-1.97, -3.9) * mm});
            skLineSegment(sketch, "E386", {"start": v(-1.97, -3.9) * mm, "end": v(-1.98, -4) * mm});
            skLineSegment(sketch, "E387", {"start": v(-1.98, -4) * mm, "end": v(-1.98, -4.14) * mm});
            skLineSegment(sketch, "E388", {"start": v(-1.98, -4.14) * mm, "end": v(-1.96, -4.28) * mm});
            skLineSegment(sketch, "E389", {"start": v(-1.96, -4.28) * mm, "end": v(-1.94, -4.44) * mm});
            skLineSegment(sketch, "E390", {"start": v(-1.94, -4.44) * mm, "end": v(-1.9, -4.62) * mm});
            skLineSegment(sketch, "E391", {"start": v(-1.9, -4.62) * mm, "end": v(-1.85, -4.8) * mm});
            skLineSegment(sketch, "E392", {"start": v(-1.85, -4.8) * mm, "end": v(-1.81, -4.92) * mm});
            skLineSegment(sketch, "E393", {"start": v(-1.81, -4.92) * mm, "end": v(-1.62, -4.99) * mm});
            skLineSegment(sketch, "E394", {"start": v(-1.62, -4.99) * mm, "end": v(-1.43, -5.04) * mm});
            skLineSegment(sketch, "E395", {"start": v(-1.43, -5.04) * mm, "end": v(-1.33, -4.97) * mm});
            skLineSegment(sketch, "E396", {"start": v(-1.33, -4.97) * mm, "end": v(-1.18, -4.85) * mm});
            skLineSegment(sketch, "E397", {"start": v(-1.18, -4.85) * mm, "end": v(-1.04, -4.74) * mm});
            skLineSegment(sketch, "E398", {"start": v(-1.04, -4.74) * mm, "end": v(-0.93, -4.62) * mm});
            skLineSegment(sketch, "E399", {"start": v(-0.93, -4.62) * mm, "end": v(-0.83, -4.51) * mm});
            skLineSegment(sketch, "E400", {"start": v(-0.83, -4.51) * mm, "end": v(-0.76, -4.4) * mm});
            skLineSegment(sketch, "E401", {"start": v(-0.76, -4.4) * mm, "end": v(-0.7, -4.31) * mm});
            skLineSegment(sketch, "E402", {"start": v(-0.7, -4.31) * mm, "end": v(-0.64, -4.23) * mm});
            skLineSegment(sketch, "E403", {"start": v(-0.64, -4.23) * mm, "end": v(-0.6, -4.15) * mm});
            skLineSegment(sketch, "E404", {"start": v(-0.6, -4.15) * mm, "end": v(-0.58, -4.1) * mm});
            skLineSegment(sketch, "E405", {"start": v(-0.58, -4.1) * mm, "end": v(-0.56, -4.04) * mm});
            skLineSegment(sketch, "E406", {"start": v(-0.56, -4.04) * mm, "end": v(-0.55, -4.01) * mm});
            skLineSegment(sketch, "E407", {"start": v(-0.55, -4.01) * mm, "end": v(-0.55, -4) * mm});
            skLineSegment(sketch, "E408", {"start": v(-0.55, -4) * mm, "end": v(-0.56, -3.9) * mm});
            skLineSegment(sketch, "E409", {"start": v(-0.56, -3.9) * mm, "end": v(-0.54, -3.76) * mm});
            skLineSegment(sketch, "E410", {"start": v(-0.54, -3.76) * mm, "end": v(-0.52, -3.63) * mm});
            skLineSegment(sketch, "E411", {"start": v(-0.52, -3.63) * mm, "end": v(-0.48, -3.53) * mm});
            skLineSegment(sketch, "E412", {"start": v(-0.48, -3.53) * mm, "end": v(-0.43, -3.44) * mm});
            skLineSegment(sketch, "E413", {"start": v(-0.43, -3.44) * mm, "end": v(-0.37, -3.37) * mm});
            skLineSegment(sketch, "E414", {"start": v(-0.37, -3.37) * mm, "end": v(-0.31, -3.32) * mm});
            skLineSegment(sketch, "E415", {"start": v(-0.31, -3.32) * mm, "end": v(-0.24, -3.3) * mm});
            skLineSegment(sketch, "E416", {"start": v(-0.24, -3.3) * mm, "end": v(-0.18, -3.3) * mm});
            skLineSegment(sketch, "E417", {"start": v(-0.18, -3.3) * mm, "end": v(-0.1, -3.3) * mm});
            skLineSegment(sketch, "E418", {"start": v(-0.1, -3.3) * mm, "end": v(0.1, -3.3) * mm});
            skLineSegment(sketch, "E419", {"start": v(0.1, -3.3) * mm, "end": v(0.18, -3.3) * mm});
            skLineSegment(sketch, "E420", {"start": v(0.18, -3.3) * mm, "end": v(0.24, -3.3) * mm});
            skLineSegment(sketch, "E421", {"start": v(0.24, -3.3) * mm, "end": v(0.31, -3.32) * mm});
            skLineSegment(sketch, "E422", {"start": v(0.31, -3.32) * mm, "end": v(0.37, -3.37) * mm});
            skLineSegment(sketch, "E423", {"start": v(0.37, -3.37) * mm, "end": v(0.43, -3.44) * mm});
            skLineSegment(sketch, "E424", {"start": v(0.43, -3.44) * mm, "end": v(0.48, -3.53) * mm});
            skLineSegment(sketch, "E425", {"start": v(0.48, -3.53) * mm, "end": v(0.52, -3.63) * mm});
            skLineSegment(sketch, "E426", {"start": v(0.52, -3.63) * mm, "end": v(0.54, -3.76) * mm});
            skLineSegment(sketch, "E427", {"start": v(0.54, -3.76) * mm, "end": v(0.56, -3.9) * mm});
            skLineSegment(sketch, "E428", {"start": v(0.56, -3.9) * mm, "end": v(0.55, -4) * mm});
            skLineSegment(sketch, "E429", {"start": v(0.55, -4) * mm, "end": v(0.55, -4.01) * mm});
            skLineSegment(sketch, "E430", {"start": v(0.55, -4.01) * mm, "end": v(0.56, -4.04) * mm});
            skLineSegment(sketch, "E431", {"start": v(0.56, -4.04) * mm, "end": v(0.58, -4.1) * mm});
            skLineSegment(sketch, "E432", {"start": v(0.58, -4.1) * mm, "end": v(0.6, -4.15) * mm});
            skLineSegment(sketch, "E433", {"start": v(0.6, -4.15) * mm, "end": v(0.64, -4.23) * mm});
            skLineSegment(sketch, "E434", {"start": v(0.64, -4.23) * mm, "end": v(0.7, -4.31) * mm});
            skLineSegment(sketch, "E435", {"start": v(0.7, -4.31) * mm, "end": v(0.76, -4.4) * mm});
            skLineSegment(sketch, "E436", {"start": v(0.76, -4.4) * mm, "end": v(0.83, -4.51) * mm});
            skLineSegment(sketch, "E437", {"start": v(0.83, -4.51) * mm, "end": v(0.93, -4.62) * mm});
            skLineSegment(sketch, "E438", {"start": v(0.93, -4.62) * mm, "end": v(1.04, -4.74) * mm});
            skLineSegment(sketch, "E439", {"start": v(1.04, -4.74) * mm, "end": v(1.18, -4.85) * mm});
            skLineSegment(sketch, "E440", {"start": v(1.18, -4.85) * mm, "end": v(1.33, -4.97) * mm});
            skLineSegment(sketch, "E441", {"start": v(1.33, -4.97) * mm, "end": v(1.43, -5.04) * mm});
            skLineSegment(sketch, "E442", {"start": v(1.43, -5.04) * mm, "end": v(1.62, -4.99) * mm});
            skLineSegment(sketch, "E443", {"start": v(1.62, -4.99) * mm, "end": v(1.81, -4.92) * mm});
            skLineSegment(sketch, "E444", {"start": v(1.81, -4.92) * mm, "end": v(1.85, -4.8) * mm});
            skLineSegment(sketch, "E445", {"start": v(1.85, -4.8) * mm, "end": v(1.9, -4.62) * mm});
            skLineSegment(sketch, "E446", {"start": v(1.9, -4.62) * mm, "end": v(1.94, -4.44) * mm});
            skLineSegment(sketch, "E447", {"start": v(1.94, -4.44) * mm, "end": v(1.96, -4.28) * mm});
            skLineSegment(sketch, "E448", {"start": v(1.96, -4.28) * mm, "end": v(1.98, -4.14) * mm});
            skLineSegment(sketch, "E449", {"start": v(1.98, -4.14) * mm, "end": v(1.98, -4) * mm});
            skLineSegment(sketch, "E450", {"start": v(1.98, -4) * mm, "end": v(1.97, -3.9) * mm});
            skLineSegment(sketch, "E451", {"start": v(1.97, -3.9) * mm, "end": v(1.96, -3.8) * mm});
            skLineSegment(sketch, "E452", {"start": v(1.96, -3.8) * mm, "end": v(1.95, -3.72) * mm});
            skLineSegment(sketch, "E453", {"start": v(1.95, -3.72) * mm, "end": v(1.94, -3.65) * mm});
            skLineSegment(sketch, "E454", {"start": v(1.94, -3.65) * mm, "end": v(1.92, -3.6) * mm});
            skLineSegment(sketch, "E455", {"start": v(1.92, -3.6) * mm, "end": v(1.9, -3.57) * mm});
            skLineSegment(sketch, "E456", {"start": v(1.9, -3.57) * mm, "end": v(1.9, -3.56) * mm});
            skLineSegment(sketch, "E457", {"start": v(1.9, -3.56) * mm, "end": v(1.85, -3.49) * mm});
            skLineSegment(sketch, "E458", {"start": v(1.85, -3.49) * mm, "end": v(1.77, -3.36) * mm});
            skLineSegment(sketch, "E459", {"start": v(1.77, -3.36) * mm, "end": v(1.72, -3.25) * mm});
            skLineSegment(sketch, "E460", {"start": v(1.72, -3.25) * mm, "end": v(1.68, -3.13) * mm});
            skLineSegment(sketch, "E461", {"start": v(1.68, -3.13) * mm, "end": v(1.67, -3.03) * mm});
            skLineSegment(sketch, "E462", {"start": v(1.67, -3.03) * mm, "end": v(1.68, -2.95) * mm});
            skLineSegment(sketch, "E463", {"start": v(1.68, -2.95) * mm, "end": v(1.7, -2.87) * mm});
            skLineSegment(sketch, "E464", {"start": v(1.7, -2.87) * mm, "end": v(1.74, -2.8) * mm});
            skLineSegment(sketch, "E465", {"start": v(1.74, -2.8) * mm, "end": v(1.8, -2.77) * mm});
            skLineSegment(sketch, "E466", {"start": v(1.8, -2.77) * mm, "end": v(1.85, -2.73) * mm});
            skLineSegment(sketch, "E467", {"start": v(1.85, -2.73) * mm, "end": v(2.02, -2.6) * mm});
            skLineSegment(sketch, "E468", {"start": v(2.02, -2.6) * mm, "end": v(2.08, -2.56) * mm});
            skLineSegment(sketch, "E469", {"start": v(2.08, -2.56) * mm, "end": v(2.13, -2.52) * mm});
            skLineSegment(sketch, "E470", {"start": v(2.13, -2.52) * mm, "end": v(2.2, -2.5) * mm});
            skLineSegment(sketch, "E471", {"start": v(2.2, -2.5) * mm, "end": v(2.28, -2.5) * mm});
            skLineSegment(sketch, "E472", {"start": v(2.28, -2.5) * mm, "end": v(2.37, -2.53) * mm});
            skLineSegment(sketch, "E473", {"start": v(2.37, -2.53) * mm, "end": v(2.46, -2.57) * mm});
            skLineSegment(sketch, "E474", {"start": v(2.46, -2.57) * mm, "end": v(2.56, -2.64) * mm});
            skLineSegment(sketch, "E475", {"start": v(2.56, -2.64) * mm, "end": v(2.65, -2.72) * mm});
            skLineSegment(sketch, "E476", {"start": v(2.65, -2.72) * mm, "end": v(2.74, -2.83) * mm});
            skLineSegment(sketch, "E477", {"start": v(2.74, -2.83) * mm, "end": v(2.8, -2.91) * mm});
            skLineSegment(sketch, "E478", {"start": v(2.8, -2.91) * mm, "end": v(2.8, -2.92) * mm});
            skLineSegment(sketch, "E479", {"start": v(2.8, -2.92) * mm, "end": v(2.83, -2.94) * mm});
            skLineSegment(sketch, "E480", {"start": v(2.83, -2.94) * mm, "end": v(2.87, -2.97) * mm});
            skLineSegment(sketch, "E481", {"start": v(2.87, -2.97) * mm, "end": v(2.93, -3) * mm});
            skLineSegment(sketch, "E482", {"start": v(2.93, -3) * mm, "end": v(3, -3.04) * mm});
            skLineSegment(sketch, "E483", {"start": v(3, -3.04) * mm, "end": v(3.1, -3.08) * mm});
            skLineSegment(sketch, "E484", {"start": v(3.1, -3.08) * mm, "end": v(3.2, -3.12) * mm});
            skLineSegment(sketch, "E485", {"start": v(3.2, -3.12) * mm, "end": v(3.33, -3.16) * mm});
            skLineSegment(sketch, "E486", {"start": v(3.33, -3.16) * mm, "end": v(3.47, -3.2) * mm});
            skLineSegment(sketch, "E487", {"start": v(3.47, -3.2) * mm, "end": v(3.63, -3.22) * mm});
            skLineSegment(sketch, "E488", {"start": v(3.63, -3.22) * mm, "end": v(3.8, -3.24) * mm});
            skLineSegment(sketch, "E489", {"start": v(3.8, -3.24) * mm, "end": v(4, -3.24) * mm});
            skLineSegment(sketch, "E490", {"start": v(4, -3.24) * mm, "end": v(4.12, -3.24) * mm});
            skLineSegment(sketch, "E491", {"start": v(0.09, -1.25) * mm, "end": v(0, -1.25) * mm});
            skLineSegment(sketch, "E492", {"start": v(0, -1.25) * mm, "end": v(-0.09, -1.25) * mm});
            skLineSegment(sketch, "E493", {"start": v(-0.09, -1.25) * mm, "end": v(-0.17, -1.24) * mm});
            skLineSegment(sketch, "E494", {"start": v(-0.17, -1.24) * mm, "end": v(-0.26, -1.22) * mm});
            skLineSegment(sketch, "E495", {"start": v(-0.26, -1.22) * mm, "end": v(-0.34, -1.2) * mm});
            skLineSegment(sketch, "E496", {"start": v(-0.34, -1.2) * mm, "end": v(-0.43, -1.17) * mm});
            skLineSegment(sketch, "E497", {"start": v(-0.43, -1.17) * mm, "end": v(-0.5, -1.14) * mm});
            skLineSegment(sketch, "E498", {"start": v(-0.5, -1.14) * mm, "end": v(-0.59, -1.1) * mm});
            skLineSegment(sketch, "E499", {"start": v(-0.59, -1.1) * mm, "end": v(-0.66, -1.06) * mm});
            skLineSegment(sketch, "E500", {"start": v(-0.66, -1.06) * mm, "end": v(-0.73, -1.01) * mm});
            skLineSegment(sketch, "E501", {"start": v(-0.73, -1.01) * mm, "end": v(-0.8, -0.96) * mm});
            skLineSegment(sketch, "E502", {"start": v(-0.8, -0.96) * mm, "end": v(-0.87, -0.9) * mm});
            skLineSegment(sketch, "E503", {"start": v(-0.87, -0.9) * mm, "end": v(-0.93, -0.84) * mm});
            skLineSegment(sketch, "E504", {"start": v(-0.93, -0.84) * mm, "end": v(-0.99, -0.77) * mm});
            skLineSegment(sketch, "E505", {"start": v(-0.99, -0.77) * mm, "end": v(-1.04, -0.7) * mm});
            skLineSegment(sketch, "E506", {"start": v(-1.04, -0.7) * mm, "end": v(-1.08, -0.62) * mm});
            skLineSegment(sketch, "E507", {"start": v(-1.08, -0.62) * mm, "end": v(-1.12, -0.55) * mm});
            skLineSegment(sketch, "E508", {"start": v(-1.12, -0.55) * mm, "end": v(-1.16, -0.47) * mm});
            skLineSegment(sketch, "E509", {"start": v(-1.16, -0.47) * mm, "end": v(-1.19, -0.39) * mm});
            skLineSegment(sketch, "E510", {"start": v(-1.19, -0.39) * mm, "end": v(-1.21, -0.3) * mm});
            skLineSegment(sketch, "E511", {"start": v(-1.21, -0.3) * mm, "end": v(-1.23, -0.22) * mm});
            skLineSegment(sketch, "E512", {"start": v(-1.23, -0.22) * mm, "end": v(-1.24, -0.13) * mm});
            skLineSegment(sketch, "E513", {"start": v(-1.24, -0.13) * mm, "end": v(-1.25, -0.04) * mm});
            skLineSegment(sketch, "E514", {"start": v(-1.25, -0.04) * mm, "end": v(-1.25, 0.04) * mm});
            skLineSegment(sketch, "E515", {"start": v(-1.25, 0.04) * mm, "end": v(-1.24, 0.13) * mm});
            skLineSegment(sketch, "E516", {"start": v(-1.24, 0.13) * mm, "end": v(-1.23, 0.22) * mm});
            skLineSegment(sketch, "E517", {"start": v(-1.23, 0.22) * mm, "end": v(-1.21, 0.3) * mm});
            skLineSegment(sketch, "E518", {"start": v(-1.21, 0.3) * mm, "end": v(-1.19, 0.39) * mm});
            skLineSegment(sketch, "E519", {"start": v(-1.19, 0.39) * mm, "end": v(-1.16, 0.47) * mm});
            skLineSegment(sketch, "E520", {"start": v(-1.16, 0.47) * mm, "end": v(-1.12, 0.55) * mm});
            skLineSegment(sketch, "E521", {"start": v(-1.12, 0.55) * mm, "end": v(-1.08, 0.62) * mm});
            skLineSegment(sketch, "E522", {"start": v(-1.08, 0.62) * mm, "end": v(-1.04, 0.7) * mm});
            skLineSegment(sketch, "E523", {"start": v(-1.04, 0.7) * mm, "end": v(-0.99, 0.77) * mm});
            skLineSegment(sketch, "E524", {"start": v(-0.99, 0.77) * mm, "end": v(-0.93, 0.84) * mm});
            skLineSegment(sketch, "E525", {"start": v(-0.93, 0.84) * mm, "end": v(-0.87, 0.9) * mm});
            skLineSegment(sketch, "E526", {"start": v(-0.87, 0.9) * mm, "end": v(-0.8, 0.96) * mm});
            skLineSegment(sketch, "E527", {"start": v(-0.8, 0.96) * mm, "end": v(-0.73, 1.01) * mm});
            skLineSegment(sketch, "E528", {"start": v(-0.73, 1.01) * mm, "end": v(-0.66, 1.06) * mm});
            skLineSegment(sketch, "E529", {"start": v(-0.66, 1.06) * mm, "end": v(-0.59, 1.1) * mm});
            skLineSegment(sketch, "E530", {"start": v(-0.59, 1.1) * mm, "end": v(-0.5, 1.14) * mm});
            skLineSegment(sketch, "E531", {"start": v(-0.5, 1.14) * mm, "end": v(-0.43, 1.17) * mm});
            skLineSegment(sketch, "E532", {"start": v(-0.43, 1.17) * mm, "end": v(-0.34, 1.2) * mm});
            skLineSegment(sketch, "E533", {"start": v(-0.34, 1.2) * mm, "end": v(-0.26, 1.22) * mm});
            skLineSegment(sketch, "E534", {"start": v(-0.26, 1.22) * mm, "end": v(-0.17, 1.24) * mm});
            skLineSegment(sketch, "E535", {"start": v(-0.17, 1.24) * mm, "end": v(-0.09, 1.25) * mm});
            skLineSegment(sketch, "E536", {"start": v(-0.09, 1.25) * mm, "end": v(0, 1.25) * mm});
            skLineSegment(sketch, "E537", {"start": v(0, 1.25) * mm, "end": v(0.09, 1.25) * mm});
            skLineSegment(sketch, "E538", {"start": v(0.09, 1.25) * mm, "end": v(0.17, 1.24) * mm});
            skLineSegment(sketch, "E539", {"start": v(0.17, 1.24) * mm, "end": v(0.26, 1.22) * mm});
            skLineSegment(sketch, "E540", {"start": v(0.26, 1.22) * mm, "end": v(0.34, 1.2) * mm});
            skLineSegment(sketch, "E541", {"start": v(0.34, 1.2) * mm, "end": v(0.43, 1.17) * mm});
            skLineSegment(sketch, "E542", {"start": v(0.43, 1.17) * mm, "end": v(0.5, 1.14) * mm});
            skLineSegment(sketch, "E543", {"start": v(0.5, 1.14) * mm, "end": v(0.59, 1.1) * mm});
            skLineSegment(sketch, "E544", {"start": v(0.59, 1.1) * mm, "end": v(0.66, 1.06) * mm});
            skLineSegment(sketch, "E545", {"start": v(0.66, 1.06) * mm, "end": v(0.73, 1.01) * mm});
            skLineSegment(sketch, "E546", {"start": v(0.73, 1.01) * mm, "end": v(0.8, 0.96) * mm});
            skLineSegment(sketch, "E547", {"start": v(0.8, 0.96) * mm, "end": v(0.87, 0.9) * mm});
            skLineSegment(sketch, "E548", {"start": v(0.87, 0.9) * mm, "end": v(0.93, 0.84) * mm});
            skLineSegment(sketch, "E549", {"start": v(0.93, 0.84) * mm, "end": v(0.99, 0.77) * mm});
            skLineSegment(sketch, "E550", {"start": v(0.99, 0.77) * mm, "end": v(1.04, 0.7) * mm});
            skLineSegment(sketch, "E551", {"start": v(1.04, 0.7) * mm, "end": v(1.08, 0.62) * mm});
            skLineSegment(sketch, "E552", {"start": v(1.08, 0.62) * mm, "end": v(1.12, 0.55) * mm});
            skLineSegment(sketch, "E553", {"start": v(1.12, 0.55) * mm, "end": v(1.16, 0.47) * mm});
            skLineSegment(sketch, "E554", {"start": v(1.16, 0.47) * mm, "end": v(1.19, 0.39) * mm});
            skLineSegment(sketch, "E555", {"start": v(1.19, 0.39) * mm, "end": v(1.21, 0.3) * mm});
            skLineSegment(sketch, "E556", {"start": v(1.21, 0.3) * mm, "end": v(1.23, 0.22) * mm});
            skLineSegment(sketch, "E557", {"start": v(1.23, 0.22) * mm, "end": v(1.24, 0.13) * mm});
            skLineSegment(sketch, "E558", {"start": v(1.24, 0.13) * mm, "end": v(1.25, 0.04) * mm});
            skLineSegment(sketch, "E559", {"start": v(1.25, 0.04) * mm, "end": v(1.25, -0.04) * mm});
            skLineSegment(sketch, "E560", {"start": v(1.25, -0.04) * mm, "end": v(1.24, -0.13) * mm});
            skLineSegment(sketch, "E561", {"start": v(1.24, -0.13) * mm, "end": v(1.23, -0.22) * mm});
            skLineSegment(sketch, "E562", {"start": v(1.23, -0.22) * mm, "end": v(1.21, -0.3) * mm});
            skLineSegment(sketch, "E563", {"start": v(1.21, -0.3) * mm, "end": v(1.19, -0.39) * mm});
            skLineSegment(sketch, "E564", {"start": v(1.19, -0.39) * mm, "end": v(1.16, -0.47) * mm});
            skLineSegment(sketch, "E565", {"start": v(1.16, -0.47) * mm, "end": v(1.12, -0.55) * mm});
            skLineSegment(sketch, "E566", {"start": v(1.12, -0.55) * mm, "end": v(1.08, -0.62) * mm});
            skLineSegment(sketch, "E567", {"start": v(1.08, -0.62) * mm, "end": v(1.04, -0.7) * mm});
            skLineSegment(sketch, "E568", {"start": v(1.04, -0.7) * mm, "end": v(0.99, -0.77) * mm});
            skLineSegment(sketch, "E569", {"start": v(0.99, -0.77) * mm, "end": v(0.93, -0.84) * mm});
            skLineSegment(sketch, "E570", {"start": v(0.93, -0.84) * mm, "end": v(0.87, -0.9) * mm});
            skLineSegment(sketch, "E571", {"start": v(0.87, -0.9) * mm, "end": v(0.8, -0.96) * mm});
            skLineSegment(sketch, "E572", {"start": v(0.8, -0.96) * mm, "end": v(0.73, -1.01) * mm});
            skLineSegment(sketch, "E573", {"start": v(0.73, -1.01) * mm, "end": v(0.66, -1.06) * mm});
            skLineSegment(sketch, "E574", {"start": v(0.66, -1.06) * mm, "end": v(0.59, -1.1) * mm});
            skLineSegment(sketch, "E575", {"start": v(0.59, -1.1) * mm, "end": v(0.5, -1.14) * mm});
            skLineSegment(sketch, "E576", {"start": v(0.5, -1.14) * mm, "end": v(0.43, -1.17) * mm});
            skLineSegment(sketch, "E577", {"start": v(0.43, -1.17) * mm, "end": v(0.34, -1.2) * mm});
            skLineSegment(sketch, "E578", {"start": v(0.34, -1.2) * mm, "end": v(0.26, -1.22) * mm});
            skLineSegment(sketch, "E579", {"start": v(0.26, -1.22) * mm, "end": v(0.17, -1.24) * mm});
            skLineSegment(sketch, "E580", {"start": v(0.17, -1.24) * mm, "end": v(0.09, -1.25) * mm});
            skLineSegment(sketch, "E581", {"start": v(3.82, 1.81) * mm, "end": v(3.75, 1.62) * mm});
            skLineSegment(sketch, "E582", {"start": v(3.75, 1.62) * mm, "end": v(3.7, 1.43) * mm});
            skLineSegment(sketch, "E583", {"start": v(3.7, 1.43) * mm, "end": v(3.77, 1.33) * mm});
            skLineSegment(sketch, "E584", {"start": v(3.77, 1.33) * mm, "end": v(3.89, 1.18) * mm});
            skLineSegment(sketch, "E585", {"start": v(3.89, 1.18) * mm, "end": v(4, 1.04) * mm});
            skLineSegment(sketch, "E586", {"start": v(4, 1.04) * mm, "end": v(4.12, 0.93) * mm});
            skLineSegment(sketch, "E587", {"start": v(4.12, 0.93) * mm, "end": v(4.23, 0.83) * mm});
            skLineSegment(sketch, "E588", {"start": v(4.23, 0.83) * mm, "end": v(4.33, 0.76) * mm});
            skLineSegment(sketch, "E589", {"start": v(4.33, 0.76) * mm, "end": v(4.43, 0.7) * mm});
            skLineSegment(sketch, "E590", {"start": v(4.43, 0.7) * mm, "end": v(4.51, 0.64) * mm});
            skLineSegment(sketch, "E591", {"start": v(4.51, 0.64) * mm, "end": v(4.59, 0.6) * mm});
            skLineSegment(sketch, "E592", {"start": v(4.59, 0.6) * mm, "end": v(4.65, 0.58) * mm});
            skLineSegment(sketch, "E593", {"start": v(4.65, 0.58) * mm, "end": v(4.7, 0.56) * mm});
            skLineSegment(sketch, "E594", {"start": v(4.7, 0.56) * mm, "end": v(4.73, 0.55) * mm});
            skLineSegment(sketch, "E595", {"start": v(4.73, 0.55) * mm, "end": v(4.74, 0.55) * mm});
            skLineSegment(sketch, "E596", {"start": v(4.74, 0.55) * mm, "end": v(4.84, 0.56) * mm});
            skLineSegment(sketch, "E597", {"start": v(4.84, 0.56) * mm, "end": v(4.98, 0.54) * mm});
            skLineSegment(sketch, "E598", {"start": v(4.98, 0.54) * mm, "end": v(5.1, 0.52) * mm});
            skLineSegment(sketch, "E599", {"start": v(5.1, 0.52) * mm, "end": v(5.21, 0.48) * mm});
            skLineSegment(sketch, "E600", {"start": v(5.21, 0.48) * mm, "end": v(5.3, 0.43) * mm});
            skLineSegment(sketch, "E601", {"start": v(5.3, 0.43) * mm, "end": v(5.37, 0.37) * mm});
            skLineSegment(sketch, "E602", {"start": v(5.37, 0.37) * mm, "end": v(5.42, 0.31) * mm});
            skLineSegment(sketch, "E603", {"start": v(5.42, 0.31) * mm, "end": v(5.44, 0.24) * mm});
            skLineSegment(sketch, "E604", {"start": v(5.44, 0.24) * mm, "end": v(5.45, 0.18) * mm});
            skLineSegment(sketch, "E605", {"start": v(5.45, 0.18) * mm, "end": v(5.44, 0.1) * mm});
            skLineSegment(sketch, "E606", {"start": v(5.44, 0.1) * mm, "end": v(5.44, -0.1) * mm});
            skLineSegment(sketch, "E607", {"start": v(5.44, -0.1) * mm, "end": v(5.45, -0.18) * mm});
            skLineSegment(sketch, "E608", {"start": v(5.45, -0.18) * mm, "end": v(5.44, -0.24) * mm});
            skLineSegment(sketch, "E609", {"start": v(5.44, -0.24) * mm, "end": v(5.42, -0.31) * mm});
            skLineSegment(sketch, "E610", {"start": v(5.42, -0.31) * mm, "end": v(5.37, -0.37) * mm});
            skLineSegment(sketch, "E611", {"start": v(5.37, -0.37) * mm, "end": v(5.3, -0.43) * mm});
            skLineSegment(sketch, "E612", {"start": v(5.3, -0.43) * mm, "end": v(5.21, -0.48) * mm});
            skLineSegment(sketch, "E613", {"start": v(5.21, -0.48) * mm, "end": v(5.1, -0.52) * mm});
            skLineSegment(sketch, "E614", {"start": v(5.1, -0.52) * mm, "end": v(4.98, -0.54) * mm});
            skLineSegment(sketch, "E615", {"start": v(4.98, -0.54) * mm, "end": v(4.84, -0.56) * mm});
            skLineSegment(sketch, "E616", {"start": v(4.84, -0.56) * mm, "end": v(4.74, -0.55) * mm});
            skLineSegment(sketch, "E617", {"start": v(4.74, -0.55) * mm, "end": v(4.73, -0.55) * mm});
            skLineSegment(sketch, "E618", {"start": v(4.73, -0.55) * mm, "end": v(4.7, -0.56) * mm});
            skLineSegment(sketch, "E619", {"start": v(4.7, -0.56) * mm, "end": v(4.65, -0.58) * mm});
            skLineSegment(sketch, "E620", {"start": v(4.65, -0.58) * mm, "end": v(4.59, -0.6) * mm});
            skLineSegment(sketch, "E621", {"start": v(4.59, -0.6) * mm, "end": v(4.51, -0.64) * mm});
            skLineSegment(sketch, "E622", {"start": v(4.51, -0.64) * mm, "end": v(4.43, -0.7) * mm});
            skLineSegment(sketch, "E623", {"start": v(4.43, -0.7) * mm, "end": v(4.33, -0.76) * mm});
            skLineSegment(sketch, "E624", {"start": v(4.33, -0.76) * mm, "end": v(4.23, -0.83) * mm});
            skLineSegment(sketch, "E625", {"start": v(4.23, -0.83) * mm, "end": v(4.12, -0.93) * mm});
            skLineSegment(sketch, "E626", {"start": v(4.12, -0.93) * mm, "end": v(4, -1.04) * mm});
            skLineSegment(sketch, "E627", {"start": v(4, -1.04) * mm, "end": v(3.89, -1.18) * mm});
            skLineSegment(sketch, "E628", {"start": v(3.89, -1.18) * mm, "end": v(3.77, -1.33) * mm});
            skLineSegment(sketch, "E629", {"start": v(3.77, -1.33) * mm, "end": v(3.7, -1.43) * mm});
            skLineSegment(sketch, "E630", {"start": v(3.7, -1.43) * mm, "end": v(3.75, -1.62) * mm});
            skLineSegment(sketch, "E631", {"start": v(3.75, -1.62) * mm, "end": v(3.82, -1.81) * mm});
            skLineSegment(sketch, "E632", {"start": v(3.82, -1.81) * mm, "end": v(3.93, -1.85) * mm});
            skLineSegment(sketch, "E633", {"start": v(3.93, -1.85) * mm, "end": v(4.12, -1.9) * mm});
            skLineSegment(sketch, "E634", {"start": v(4.12, -1.9) * mm, "end": v(4.3, -1.94) * mm});
            skLineSegment(sketch, "E635", {"start": v(4.3, -1.94) * mm, "end": v(4.46, -1.96) * mm});
            skLineSegment(sketch, "E636", {"start": v(4.46, -1.96) * mm, "end": v(4.6, -1.98) * mm});
            skLineSegment(sketch, "E637", {"start": v(4.6, -1.98) * mm, "end": v(4.73, -1.98) * mm});
            skLineSegment(sketch, "E638", {"start": v(4.73, -1.98) * mm, "end": v(4.84, -1.97) * mm});
            skLineSegment(sketch, "E639", {"start": v(4.84, -1.97) * mm, "end": v(4.94, -1.96) * mm});
            skLineSegment(sketch, "E640", {"start": v(4.94, -1.96) * mm, "end": v(5.02, -1.95) * mm});
            skLineSegment(sketch, "E641", {"start": v(5.02, -1.95) * mm, "end": v(5.09, -1.94) * mm});
            skLineSegment(sketch, "E642", {"start": v(5.09, -1.94) * mm, "end": v(5.14, -1.92) * mm});
            skLineSegment(sketch, "E643", {"start": v(5.14, -1.92) * mm, "end": v(5.17, -1.9) * mm});
            skLineSegment(sketch, "E644", {"start": v(5.17, -1.9) * mm, "end": v(5.18, -1.9) * mm});
            skLineSegment(sketch, "E645", {"start": v(5.18, -1.9) * mm, "end": v(5.25, -1.85) * mm});
            skLineSegment(sketch, "E646", {"start": v(5.25, -1.85) * mm, "end": v(5.38, -1.77) * mm});
            skLineSegment(sketch, "E647", {"start": v(5.38, -1.77) * mm, "end": v(5.5, -1.72) * mm});
            skLineSegment(sketch, "E648", {"start": v(5.5, -1.72) * mm, "end": v(5.6, -1.68) * mm});
            skLineSegment(sketch, "E649", {"start": v(5.6, -1.68) * mm, "end": v(5.7, -1.67) * mm});
            skLineSegment(sketch, "E650", {"start": v(5.7, -1.67) * mm, "end": v(5.8, -1.68) * mm});
            skLineSegment(sketch, "E651", {"start": v(5.8, -1.68) * mm, "end": v(5.87, -1.7) * mm});
            skLineSegment(sketch, "E652", {"start": v(5.87, -1.7) * mm, "end": v(5.93, -1.74) * mm});
            skLineSegment(sketch, "E653", {"start": v(5.93, -1.74) * mm, "end": v(5.97, -1.8) * mm});
            skLineSegment(sketch, "E654", {"start": v(5.97, -1.8) * mm, "end": v(6.01, -1.85) * mm});
            skLineSegment(sketch, "E655", {"start": v(6.01, -1.85) * mm, "end": v(6.13, -2.02) * mm});
            skLineSegment(sketch, "E656", {"start": v(6.13, -2.02) * mm, "end": v(6.18, -2.08) * mm});
            skLineSegment(sketch, "E657", {"start": v(6.18, -2.08) * mm, "end": v(6.22, -2.13) * mm});
            skLineSegment(sketch, "E658", {"start": v(6.22, -2.13) * mm, "end": v(6.23, -2.2) * mm});
            skLineSegment(sketch, "E659", {"start": v(6.23, -2.2) * mm, "end": v(6.23, -2.28) * mm});
            skLineSegment(sketch, "E660", {"start": v(6.23, -2.28) * mm, "end": v(6.21, -2.37) * mm});
            skLineSegment(sketch, "E661", {"start": v(6.21, -2.37) * mm, "end": v(6.17, -2.46) * mm});
            skLineSegment(sketch, "E662", {"start": v(6.17, -2.46) * mm, "end": v(6.1, -2.56) * mm});
            skLineSegment(sketch, "E663", {"start": v(6.1, -2.56) * mm, "end": v(6.02, -2.65) * mm});
            skLineSegment(sketch, "E664", {"start": v(6.02, -2.65) * mm, "end": v(5.9, -2.74) * mm});
            skLineSegment(sketch, "E665", {"start": v(5.9, -2.74) * mm, "end": v(5.83, -2.8) * mm});
            skLineSegment(sketch, "E666", {"start": v(5.83, -2.8) * mm, "end": v(5.82, -2.8) * mm});
            skLineSegment(sketch, "E667", {"start": v(5.82, -2.8) * mm, "end": v(5.8, -2.83) * mm});
            skLineSegment(sketch, "E668", {"start": v(5.8, -2.83) * mm, "end": v(5.77, -2.87) * mm});
            skLineSegment(sketch, "E669", {"start": v(5.77, -2.87) * mm, "end": v(5.74, -2.93) * mm});
            skLineSegment(sketch, "E670", {"start": v(5.74, -2.93) * mm, "end": v(5.7, -3) * mm});
            skLineSegment(sketch, "E671", {"start": v(5.7, -3) * mm, "end": v(5.66, -3.1) * mm});
            skLineSegment(sketch, "E672", {"start": v(5.66, -3.1) * mm, "end": v(5.62, -3.2) * mm});
            skLineSegment(sketch, "E673", {"start": v(5.62, -3.2) * mm, "end": v(5.58, -3.33) * mm});
            skLineSegment(sketch, "E674", {"start": v(5.58, -3.33) * mm, "end": v(5.55, -3.47) * mm});
            skLineSegment(sketch, "E675", {"start": v(5.55, -3.47) * mm, "end": v(5.52, -3.63) * mm});
            skLineSegment(sketch, "E676", {"start": v(5.52, -3.63) * mm, "end": v(5.5, -3.8) * mm});
            skLineSegment(sketch, "E677", {"start": v(5.5, -3.8) * mm, "end": v(5.5, -4) * mm});
            skLineSegment(sketch, "E678", {"start": v(5.5, -4) * mm, "end": v(5.5, -4.12) * mm});
            skLineSegment(sketch, "E679", {"start": v(5.5, -4.12) * mm, "end": v(5.66, -4.24) * mm});
            skLineSegment(sketch, "E680", {"start": v(5.66, -4.24) * mm, "end": v(5.82, -4.36) * mm});
            skLineSegment(sketch, "E681", {"start": v(5.82, -4.36) * mm, "end": v(5.94, -4.32) * mm});
            skLineSegment(sketch, "E682", {"start": v(5.94, -4.32) * mm, "end": v(6.12, -4.25) * mm});
            skLineSegment(sketch, "E683", {"start": v(6.12, -4.25) * mm, "end": v(6.28, -4.18) * mm});
            skLineSegment(sketch, "E684", {"start": v(6.28, -4.18) * mm, "end": v(6.43, -4.1) * mm});
            skLineSegment(sketch, "E685", {"start": v(6.43, -4.1) * mm, "end": v(6.55, -4.03) * mm});
            skLineSegment(sketch, "E686", {"start": v(6.55, -4.03) * mm, "end": v(6.66, -3.96) * mm});
            skLineSegment(sketch, "E687", {"start": v(6.66, -3.96) * mm, "end": v(6.75, -3.89) * mm});
            skLineSegment(sketch, "E688", {"start": v(6.75, -3.89) * mm, "end": v(6.82, -3.82) * mm});
            skLineSegment(sketch, "E689", {"start": v(6.82, -3.82) * mm, "end": v(6.88, -3.76) * mm});
            skLineSegment(sketch, "E690", {"start": v(6.88, -3.76) * mm, "end": v(6.92, -3.71) * mm});
            skLineSegment(sketch, "E691", {"start": v(6.92, -3.71) * mm, "end": v(6.95, -3.67) * mm});
            skLineSegment(sketch, "E692", {"start": v(6.95, -3.67) * mm, "end": v(6.97, -3.64) * mm});
            skLineSegment(sketch, "E693", {"start": v(6.97, -3.64) * mm, "end": v(6.98, -3.64) * mm});
            skLineSegment(sketch, "E694", {"start": v(6.98, -3.64) * mm, "end": v(7, -3.54) * mm});
            skLineSegment(sketch, "E695", {"start": v(7, -3.54) * mm, "end": v(7.06, -3.4) * mm});
            skLineSegment(sketch, "E696", {"start": v(7.06, -3.4) * mm, "end": v(7.12, -3.3) * mm});
            skLineSegment(sketch, "E697", {"start": v(7.12, -3.3) * mm, "end": v(7.2, -3.2) * mm});
            skLineSegment(sketch, "E698", {"start": v(7.2, -3.2) * mm, "end": v(7.27, -3.14) * mm});
            skLineSegment(sketch, "E699", {"start": v(7.27, -3.14) * mm, "end": v(7.34, -3.09) * mm});
            skLineSegment(sketch, "E700", {"start": v(7.34, -3.09) * mm, "end": v(7.42, -3.06) * mm});
            skLineSegment(sketch, "E701", {"start": v(7.42, -3.06) * mm, "end": v(7.49, -3.06) * mm});
            skLineSegment(sketch, "E702", {"start": v(7.49, -3.06) * mm, "end": v(7.56, -3.08) * mm});
            skLineSegment(sketch, "E703", {"start": v(7.56, -3.08) * mm, "end": v(7.62, -3.1) * mm});
            skLineSegment(sketch, "E704", {"start": v(7.62, -3.1) * mm, "end": v(7.82, -3.17) * mm});
            skLineSegment(sketch, "E705", {"start": v(7.82, -3.17) * mm, "end": v(7.9, -3.18) * mm});
            skLineSegment(sketch, "E706", {"start": v(7.9, -3.18) * mm, "end": v(7.95, -3.2) * mm});
            skLineSegment(sketch, "E707", {"start": v(7.95, -3.2) * mm, "end": v(8, -3.26) * mm});
            skLineSegment(sketch, "E708", {"start": v(8, -3.26) * mm, "end": v(8.05, -3.32) * mm});
            skLineSegment(sketch, "E709", {"start": v(8.05, -3.32) * mm, "end": v(8.09, -3.4) * mm});
            skLineSegment(sketch, "E710", {"start": v(8.09, -3.4) * mm, "end": v(8.1, -3.5) * mm});
            skLineSegment(sketch, "E711", {"start": v(8.1, -3.5) * mm, "end": v(8.11, -3.62) * mm});
            skLineSegment(sketch, "E712", {"start": v(8.11, -3.62) * mm, "end": v(8.1, -3.75) * mm});
            skLineSegment(sketch, "E713", {"start": v(8.1, -3.75) * mm, "end": v(8.06, -3.89) * mm});
            skLineSegment(sketch, "E714", {"start": v(8.06, -3.89) * mm, "end": v(8.03, -3.98) * mm});
            skLineSegment(sketch, "E715", {"start": v(8.03, -3.98) * mm, "end": v(8.03, -3.99) * mm});
            skLineSegment(sketch, "E716", {"start": v(8.03, -3.99) * mm, "end": v(8.03, -4.02) * mm});
            skLineSegment(sketch, "E717", {"start": v(8.03, -4.02) * mm, "end": v(8.03, -4.07) * mm});
            skLineSegment(sketch, "E718", {"start": v(8.03, -4.07) * mm, "end": v(8.03, -4.14) * mm});
            skLineSegment(sketch, "E719", {"start": v(8.03, -4.14) * mm, "end": v(8.04, -4.22) * mm});
            skLineSegment(sketch, "E720", {"start": v(8.04, -4.22) * mm, "end": v(8.07, -4.31) * mm});
            skLineSegment(sketch, "E721", {"start": v(8.07, -4.31) * mm, "end": v(8.1, -4.42) * mm});
            skLineSegment(sketch, "E722", {"start": v(8.1, -4.42) * mm, "end": v(8.14, -4.55) * mm});
            skLineSegment(sketch, "E723", {"start": v(8.14, -4.55) * mm, "end": v(8.2, -4.68) * mm});
            skLineSegment(sketch, "E724", {"start": v(8.2, -4.68) * mm, "end": v(8.27, -4.83) * mm});
            skLineSegment(sketch, "E725", {"start": v(8.27, -4.83) * mm, "end": v(8.36, -4.98) * mm});
            skLineSegment(sketch, "E726", {"start": v(8.36, -4.98) * mm, "end": v(8.47, -5.14) * mm});
            skLineSegment(sketch, "E727", {"start": v(8.47, -5.14) * mm, "end": v(8.54, -5.24) * mm});
            skLineSegment(sketch, "E728", {"start": v(8.54, -5.24) * mm, "end": v(8.74, -5.24) * mm});
            skLineSegment(sketch, "E729", {"start": v(8.74, -5.24) * mm, "end": v(8.94, -5.24) * mm});
            skLineSegment(sketch, "E730", {"start": v(8.94, -5.24) * mm, "end": v(9.01, -5.14) * mm});
            skLineSegment(sketch, "E731", {"start": v(9.01, -5.14) * mm, "end": v(9.12, -4.98) * mm});
            skLineSegment(sketch, "E732", {"start": v(9.12, -4.98) * mm, "end": v(9.21, -4.83) * mm});
            skLineSegment(sketch, "E733", {"start": v(9.21, -4.83) * mm, "end": v(9.28, -4.68) * mm});
            skLineSegment(sketch, "E734", {"start": v(9.28, -4.68) * mm, "end": v(9.34, -4.55) * mm});
            skLineSegment(sketch, "E735", {"start": v(9.34, -4.55) * mm, "end": v(9.38, -4.42) * mm});
            skLineSegment(sketch, "E736", {"start": v(9.38, -4.42) * mm, "end": v(9.41, -4.31) * mm});
            skLineSegment(sketch, "E737", {"start": v(9.41, -4.31) * mm, "end": v(9.44, -4.22) * mm});
            skLineSegment(sketch, "E738", {"start": v(9.44, -4.22) * mm, "end": v(9.45, -4.14) * mm});
            skLineSegment(sketch, "E739", {"start": v(9.45, -4.14) * mm, "end": v(9.45, -4.07) * mm});
            skLineSegment(sketch, "E740", {"start": v(9.45, -4.07) * mm, "end": v(9.45, -4.02) * mm});
            skLineSegment(sketch, "E741", {"start": v(9.45, -4.02) * mm, "end": v(9.45, -3.99) * mm});
            skLineSegment(sketch, "E742", {"start": v(9.45, -3.99) * mm, "end": v(9.45, -3.98) * mm});
            skLineSegment(sketch, "E743", {"start": v(9.45, -3.98) * mm, "end": v(9.42, -3.89) * mm});
            skLineSegment(sketch, "E744", {"start": v(9.42, -3.89) * mm, "end": v(9.38, -3.75) * mm});
            skLineSegment(sketch, "E745", {"start": v(9.38, -3.75) * mm, "end": v(9.37, -3.62) * mm});
            skLineSegment(sketch, "E746", {"start": v(9.37, -3.62) * mm, "end": v(9.37, -3.5) * mm});
            skLineSegment(sketch, "E747", {"start": v(9.37, -3.5) * mm, "end": v(9.4, -3.4) * mm});
            skLineSegment(sketch, "E748", {"start": v(9.4, -3.4) * mm, "end": v(9.43, -3.32) * mm});
            skLineSegment(sketch, "E749", {"start": v(9.43, -3.32) * mm, "end": v(9.47, -3.26) * mm});
            skLineSegment(sketch, "E750", {"start": v(9.47, -3.26) * mm, "end": v(9.53, -3.2) * mm});
            skLineSegment(sketch, "E751", {"start": v(9.53, -3.2) * mm, "end": v(9.59, -3.18) * mm});
            skLineSegment(sketch, "E752", {"start": v(9.59, -3.18) * mm, "end": v(9.66, -3.17) * mm});
            skLineSegment(sketch, "E753", {"start": v(9.66, -3.17) * mm, "end": v(9.86, -3.1) * mm});
            skLineSegment(sketch, "E754", {"start": v(9.86, -3.1) * mm, "end": v(9.92, -3.08) * mm});
            skLineSegment(sketch, "E755", {"start": v(9.92, -3.08) * mm, "end": v(10, -3.06) * mm});
            skLineSegment(sketch, "E756", {"start": v(10, -3.06) * mm, "end": v(10.06, -3.06) * mm});
            skLineSegment(sketch, "E757", {"start": v(10.06, -3.06) * mm, "end": v(10.14, -3.09) * mm});
            skLineSegment(sketch, "E758", {"start": v(10.14, -3.09) * mm, "end": v(10.21, -3.14) * mm});
            skLineSegment(sketch, "E759", {"start": v(10.21, -3.14) * mm, "end": v(10.29, -3.2) * mm});
            skLineSegment(sketch, "E760", {"start": v(10.29, -3.2) * mm, "end": v(10.36, -3.3) * mm});
            skLineSegment(sketch, "E761", {"start": v(10.36, -3.3) * mm, "end": v(10.42, -3.4) * mm});
            skLineSegment(sketch, "E762", {"start": v(10.42, -3.4) * mm, "end": v(10.48, -3.54) * mm});
            skLineSegment(sketch, "E763", {"start": v(10.48, -3.54) * mm, "end": v(10.5, -3.64) * mm});
            skLineSegment(sketch, "E764", {"start": v(10.5, -3.64) * mm, "end": v(10.5, -3.64) * mm});
            skLineSegment(sketch, "E765", {"start": v(10.5, -3.64) * mm, "end": v(10.53, -3.67) * mm});
            skLineSegment(sketch, "E766", {"start": v(10.53, -3.67) * mm, "end": v(10.56, -3.71) * mm});
            skLineSegment(sketch, "E767", {"start": v(10.56, -3.71) * mm, "end": v(10.6, -3.76) * mm});
            skLineSegment(sketch, "E768", {"start": v(10.6, -3.76) * mm, "end": v(10.66, -3.82) * mm});
            skLineSegment(sketch, "E769", {"start": v(10.66, -3.82) * mm, "end": v(10.73, -3.89) * mm});
            skLineSegment(sketch, "E770", {"start": v(10.73, -3.89) * mm, "end": v(10.82, -3.96) * mm});
            skLineSegment(sketch, "E771", {"start": v(10.82, -3.96) * mm, "end": v(10.93, -4.03) * mm});
            skLineSegment(sketch, "E772", {"start": v(10.93, -4.03) * mm, "end": v(11.05, -4.1) * mm});
            skLineSegment(sketch, "E773", {"start": v(11.05, -4.1) * mm, "end": v(11.2, -4.18) * mm});
            skLineSegment(sketch, "E774", {"start": v(11.2, -4.18) * mm, "end": v(11.36, -4.25) * mm});
            skLineSegment(sketch, "E775", {"start": v(11.36, -4.25) * mm, "end": v(11.54, -4.32) * mm});
            skLineSegment(sketch, "E776", {"start": v(11.54, -4.32) * mm, "end": v(11.66, -4.36) * mm});
            skLineSegment(sketch, "E777", {"start": v(11.66, -4.36) * mm, "end": v(11.82, -4.24) * mm});
            skLineSegment(sketch, "E778", {"start": v(11.82, -4.24) * mm, "end": v(11.98, -4.12) * mm});
            skLineSegment(sketch, "E779", {"start": v(11.98, -4.12) * mm, "end": v(11.98, -4) * mm});
            skLineSegment(sketch, "E780", {"start": v(11.98, -4) * mm, "end": v(11.98, -3.8) * mm});
            skLineSegment(sketch, "E781", {"start": v(11.98, -3.8) * mm, "end": v(11.96, -3.63) * mm});
            skLineSegment(sketch, "E782", {"start": v(11.96, -3.63) * mm, "end": v(11.93, -3.47) * mm});
            skLineSegment(sketch, "E783", {"start": v(11.93, -3.47) * mm, "end": v(11.9, -3.33) * mm});
            skLineSegment(sketch, "E784", {"start": v(11.9, -3.33) * mm, "end": v(11.86, -3.2) * mm});
            skLineSegment(sketch, "E785", {"start": v(11.86, -3.2) * mm, "end": v(11.82, -3.1) * mm});
            skLineSegment(sketch, "E786", {"start": v(11.82, -3.1) * mm, "end": v(11.78, -3) * mm});
            skLineSegment(sketch, "E787", {"start": v(11.78, -3) * mm, "end": v(11.74, -2.93) * mm});
            skLineSegment(sketch, "E788", {"start": v(11.74, -2.93) * mm, "end": v(11.7, -2.87) * mm});
            skLineSegment(sketch, "E789", {"start": v(11.7, -2.87) * mm, "end": v(11.68, -2.83) * mm});
            skLineSegment(sketch, "E790", {"start": v(11.68, -2.83) * mm, "end": v(11.66, -2.8) * mm});
            skLineSegment(sketch, "E791", {"start": v(11.66, -2.8) * mm, "end": v(11.65, -2.8) * mm});
            skLineSegment(sketch, "E792", {"start": v(11.65, -2.8) * mm, "end": v(11.57, -2.74) * mm});
            skLineSegment(sketch, "E793", {"start": v(11.57, -2.74) * mm, "end": v(11.46, -2.65) * mm});
            skLineSegment(sketch, "E794", {"start": v(11.46, -2.65) * mm, "end": v(11.38, -2.56) * mm});
            skLineSegment(sketch, "E795", {"start": v(11.38, -2.56) * mm, "end": v(11.31, -2.46) * mm});
            skLineSegment(sketch, "E796", {"start": v(11.31, -2.46) * mm, "end": v(11.27, -2.37) * mm});
            skLineSegment(sketch, "E797", {"start": v(11.27, -2.37) * mm, "end": v(11.25, -2.28) * mm});
            skLineSegment(sketch, "E798", {"start": v(11.25, -2.28) * mm, "end": v(11.25, -2.2) * mm});
            skLineSegment(sketch, "E799", {"start": v(11.25, -2.2) * mm, "end": v(11.26, -2.13) * mm});
            skLineSegment(sketch, "E800", {"start": v(11.26, -2.13) * mm, "end": v(11.3, -2.08) * mm});
            skLineSegment(sketch, "E801", {"start": v(11.3, -2.08) * mm, "end": v(11.35, -2.02) * mm});
            skLineSegment(sketch, "E802", {"start": v(11.35, -2.02) * mm, "end": v(11.47, -1.85) * mm});
            skLineSegment(sketch, "E803", {"start": v(11.47, -1.85) * mm, "end": v(11.5, -1.8) * mm});
            skLineSegment(sketch, "E804", {"start": v(11.5, -1.8) * mm, "end": v(11.55, -1.74) * mm});
            skLineSegment(sketch, "E805", {"start": v(11.55, -1.74) * mm, "end": v(11.6, -1.7) * mm});
            skLineSegment(sketch, "E806", {"start": v(11.6, -1.7) * mm, "end": v(11.69, -1.68) * mm});
            skLineSegment(sketch, "E807", {"start": v(11.69, -1.68) * mm, "end": v(11.77, -1.67) * mm});
            skLineSegment(sketch, "E808", {"start": v(11.77, -1.67) * mm, "end": v(11.87, -1.68) * mm});
            skLineSegment(sketch, "E809", {"start": v(11.87, -1.68) * mm, "end": v(11.99, -1.72) * mm});
            skLineSegment(sketch, "E810", {"start": v(11.99, -1.72) * mm, "end": v(12.1, -1.77) * mm});
            skLineSegment(sketch, "E811", {"start": v(12.1, -1.77) * mm, "end": v(12.23, -1.85) * mm});
            skLineSegment(sketch, "E812", {"start": v(12.23, -1.85) * mm, "end": v(12.3, -1.9) * mm});
            skLineSegment(sketch, "E813", {"start": v(12.3, -1.9) * mm, "end": v(12.3, -1.9) * mm});
            skLineSegment(sketch, "E814", {"start": v(12.3, -1.9) * mm, "end": v(12.34, -1.92) * mm});
            skLineSegment(sketch, "E815", {"start": v(12.34, -1.92) * mm, "end": v(12.4, -1.94) * mm});
            skLineSegment(sketch, "E816", {"start": v(12.4, -1.94) * mm, "end": v(12.46, -1.95) * mm});
            skLineSegment(sketch, "E817", {"start": v(12.46, -1.95) * mm, "end": v(12.54, -1.96) * mm});
            skLineSegment(sketch, "E818", {"start": v(12.54, -1.96) * mm, "end": v(12.64, -1.97) * mm});
            skLineSegment(sketch, "E819", {"start": v(12.64, -1.97) * mm, "end": v(12.75, -1.98) * mm});
            skLineSegment(sketch, "E820", {"start": v(12.75, -1.98) * mm, "end": v(12.88, -1.98) * mm});
            skLineSegment(sketch, "E821", {"start": v(12.88, -1.98) * mm, "end": v(13.02, -1.96) * mm});
            skLineSegment(sketch, "E822", {"start": v(13.02, -1.96) * mm, "end": v(13.18, -1.94) * mm});
            skLineSegment(sketch, "E823", {"start": v(13.18, -1.94) * mm, "end": v(13.36, -1.9) * mm});
            skLineSegment(sketch, "E824", {"start": v(13.36, -1.9) * mm, "end": v(13.55, -1.85) * mm});
            skLineSegment(sketch, "E825", {"start": v(13.55, -1.85) * mm, "end": v(13.66, -1.81) * mm});
            skLineSegment(sketch, "E826", {"start": v(13.66, -1.81) * mm, "end": v(13.73, -1.62) * mm});
            skLineSegment(sketch, "E827", {"start": v(13.73, -1.62) * mm, "end": v(13.78, -1.43) * mm});
            skLineSegment(sketch, "E828", {"start": v(13.78, -1.43) * mm, "end": v(13.71, -1.33) * mm});
            skLineSegment(sketch, "E829", {"start": v(13.71, -1.33) * mm, "end": v(13.6, -1.18) * mm});
            skLineSegment(sketch, "E830", {"start": v(13.6, -1.18) * mm, "end": v(13.48, -1.04) * mm});
            skLineSegment(sketch, "E831", {"start": v(13.48, -1.04) * mm, "end": v(13.36, -0.93) * mm});
            skLineSegment(sketch, "E832", {"start": v(13.36, -0.93) * mm, "end": v(13.25, -0.83) * mm});
            skLineSegment(sketch, "E833", {"start": v(13.25, -0.83) * mm, "end": v(13.15, -0.76) * mm});
            skLineSegment(sketch, "E834", {"start": v(13.15, -0.76) * mm, "end": v(13.05, -0.7) * mm});
            skLineSegment(sketch, "E835", {"start": v(13.05, -0.7) * mm, "end": v(12.97, -0.64) * mm});
            skLineSegment(sketch, "E836", {"start": v(12.97, -0.64) * mm, "end": v(12.9, -0.6) * mm});
            skLineSegment(sketch, "E837", {"start": v(12.9, -0.6) * mm, "end": v(12.83, -0.58) * mm});
            skLineSegment(sketch, "E838", {"start": v(12.83, -0.58) * mm, "end": v(12.78, -0.56) * mm});
            skLineSegment(sketch, "E839", {"start": v(12.78, -0.56) * mm, "end": v(12.75, -0.55) * mm});
            skLineSegment(sketch, "E840", {"start": v(12.75, -0.55) * mm, "end": v(12.74, -0.55) * mm});
            skLineSegment(sketch, "E841", {"start": v(12.74, -0.55) * mm, "end": v(12.64, -0.56) * mm});
            skLineSegment(sketch, "E842", {"start": v(12.64, -0.56) * mm, "end": v(12.5, -0.54) * mm});
            skLineSegment(sketch, "E843", {"start": v(12.5, -0.54) * mm, "end": v(12.37, -0.52) * mm});
            skLineSegment(sketch, "E844", {"start": v(12.37, -0.52) * mm, "end": v(12.27, -0.48) * mm});
            skLineSegment(sketch, "E845", {"start": v(12.27, -0.48) * mm, "end": v(12.18, -0.43) * mm});
            skLineSegment(sketch, "E846", {"start": v(12.18, -0.43) * mm, "end": v(12.1, -0.37) * mm});
            skLineSegment(sketch, "E847", {"start": v(12.1, -0.37) * mm, "end": v(12.06, -0.31) * mm});
            skLineSegment(sketch, "E848", {"start": v(12.06, -0.31) * mm, "end": v(12.04, -0.24) * mm});
            skLineSegment(sketch, "E849", {"start": v(12.04, -0.24) * mm, "end": v(12.03, -0.18) * mm});
            skLineSegment(sketch, "E850", {"start": v(12.03, -0.18) * mm, "end": v(12.04, -0.1) * mm});
            skLineSegment(sketch, "E851", {"start": v(12.04, -0.1) * mm, "end": v(12.04, 0.1) * mm});
            skLineSegment(sketch, "E852", {"start": v(12.04, 0.1) * mm, "end": v(12.03, 0.18) * mm});
            skLineSegment(sketch, "E853", {"start": v(12.03, 0.18) * mm, "end": v(12.04, 0.24) * mm});
            skLineSegment(sketch, "E854", {"start": v(12.04, 0.24) * mm, "end": v(12.06, 0.31) * mm});
            skLineSegment(sketch, "E855", {"start": v(12.06, 0.31) * mm, "end": v(12.1, 0.37) * mm});
            skLineSegment(sketch, "E856", {"start": v(12.1, 0.37) * mm, "end": v(12.18, 0.43) * mm});
            skLineSegment(sketch, "E857", {"start": v(12.18, 0.43) * mm, "end": v(12.27, 0.48) * mm});
            skLineSegment(sketch, "E858", {"start": v(12.27, 0.48) * mm, "end": v(12.37, 0.52) * mm});
            skLineSegment(sketch, "E859", {"start": v(12.37, 0.52) * mm, "end": v(12.5, 0.54) * mm});
            skLineSegment(sketch, "E860", {"start": v(12.5, 0.54) * mm, "end": v(12.64, 0.56) * mm});
            skLineSegment(sketch, "E861", {"start": v(12.64, 0.56) * mm, "end": v(12.74, 0.55) * mm});
            skLineSegment(sketch, "E862", {"start": v(12.74, 0.55) * mm, "end": v(12.75, 0.55) * mm});
            skLineSegment(sketch, "E863", {"start": v(12.75, 0.55) * mm, "end": v(12.78, 0.56) * mm});
            skLineSegment(sketch, "E864", {"start": v(12.78, 0.56) * mm, "end": v(12.83, 0.58) * mm});
            skLineSegment(sketch, "E865", {"start": v(12.83, 0.58) * mm, "end": v(12.9, 0.6) * mm});
            skLineSegment(sketch, "E866", {"start": v(12.9, 0.6) * mm, "end": v(12.97, 0.64) * mm});
            skLineSegment(sketch, "E867", {"start": v(12.97, 0.64) * mm, "end": v(13.05, 0.7) * mm});
            skLineSegment(sketch, "E868", {"start": v(13.05, 0.7) * mm, "end": v(13.15, 0.76) * mm});
            skLineSegment(sketch, "E869", {"start": v(13.15, 0.76) * mm, "end": v(13.25, 0.83) * mm});
            skLineSegment(sketch, "E870", {"start": v(13.25, 0.83) * mm, "end": v(13.36, 0.93) * mm});
            skLineSegment(sketch, "E871", {"start": v(13.36, 0.93) * mm, "end": v(13.48, 1.04) * mm});
            skLineSegment(sketch, "E872", {"start": v(13.48, 1.04) * mm, "end": v(13.6, 1.18) * mm});
            skLineSegment(sketch, "E873", {"start": v(13.6, 1.18) * mm, "end": v(13.71, 1.33) * mm});
            skLineSegment(sketch, "E874", {"start": v(13.71, 1.33) * mm, "end": v(13.78, 1.43) * mm});
            skLineSegment(sketch, "E875", {"start": v(13.78, 1.43) * mm, "end": v(13.73, 1.62) * mm});
            skLineSegment(sketch, "E876", {"start": v(13.73, 1.62) * mm, "end": v(13.66, 1.81) * mm});
            skLineSegment(sketch, "E877", {"start": v(13.66, 1.81) * mm, "end": v(13.55, 1.85) * mm});
            skLineSegment(sketch, "E878", {"start": v(13.55, 1.85) * mm, "end": v(13.36, 1.9) * mm});
            skLineSegment(sketch, "E879", {"start": v(13.36, 1.9) * mm, "end": v(13.18, 1.94) * mm});
            skLineSegment(sketch, "E880", {"start": v(13.18, 1.94) * mm, "end": v(13.02, 1.96) * mm});
            skLineSegment(sketch, "E881", {"start": v(13.02, 1.96) * mm, "end": v(12.88, 1.98) * mm});
            skLineSegment(sketch, "E882", {"start": v(12.88, 1.98) * mm, "end": v(12.75, 1.98) * mm});
            skLineSegment(sketch, "E883", {"start": v(12.75, 1.98) * mm, "end": v(12.64, 1.97) * mm});
            skLineSegment(sketch, "E884", {"start": v(12.64, 1.97) * mm, "end": v(12.54, 1.96) * mm});
            skLineSegment(sketch, "E885", {"start": v(12.54, 1.96) * mm, "end": v(12.46, 1.95) * mm});
            skLineSegment(sketch, "E886", {"start": v(12.46, 1.95) * mm, "end": v(12.4, 1.94) * mm});
            skLineSegment(sketch, "E887", {"start": v(12.4, 1.94) * mm, "end": v(12.34, 1.92) * mm});
            skLineSegment(sketch, "E888", {"start": v(12.34, 1.92) * mm, "end": v(12.3, 1.9) * mm});
            skLineSegment(sketch, "E889", {"start": v(12.3, 1.9) * mm, "end": v(12.3, 1.9) * mm});
            skLineSegment(sketch, "E890", {"start": v(12.3, 1.9) * mm, "end": v(12.23, 1.85) * mm});
            skLineSegment(sketch, "E891", {"start": v(12.23, 1.85) * mm, "end": v(12.1, 1.77) * mm});
            skLineSegment(sketch, "E892", {"start": v(12.1, 1.77) * mm, "end": v(11.99, 1.72) * mm});
            skLineSegment(sketch, "E893", {"start": v(11.99, 1.72) * mm, "end": v(11.87, 1.68) * mm});
            skLineSegment(sketch, "E894", {"start": v(11.87, 1.68) * mm, "end": v(11.77, 1.67) * mm});
            skLineSegment(sketch, "E895", {"start": v(11.77, 1.67) * mm, "end": v(11.69, 1.68) * mm});
            skLineSegment(sketch, "E896", {"start": v(11.69, 1.68) * mm, "end": v(11.6, 1.7) * mm});
            skLineSegment(sketch, "E897", {"start": v(11.6, 1.7) * mm, "end": v(11.55, 1.74) * mm});
            skLineSegment(sketch, "E898", {"start": v(11.55, 1.74) * mm, "end": v(11.5, 1.8) * mm});
            skLineSegment(sketch, "E899", {"start": v(11.5, 1.8) * mm, "end": v(11.47, 1.85) * mm});
            skLineSegment(sketch, "E900", {"start": v(11.47, 1.85) * mm, "end": v(11.35, 2.02) * mm});
            skLineSegment(sketch, "E901", {"start": v(11.35, 2.02) * mm, "end": v(11.3, 2.08) * mm});
            skLineSegment(sketch, "E902", {"start": v(11.3, 2.08) * mm, "end": v(11.26, 2.13) * mm});
            skLineSegment(sketch, "E903", {"start": v(11.26, 2.13) * mm, "end": v(11.25, 2.2) * mm});
            skLineSegment(sketch, "E904", {"start": v(11.25, 2.2) * mm, "end": v(11.25, 2.28) * mm});
            skLineSegment(sketch, "E905", {"start": v(11.25, 2.28) * mm, "end": v(11.27, 2.37) * mm});
            skLineSegment(sketch, "E906", {"start": v(11.27, 2.37) * mm, "end": v(11.31, 2.46) * mm});
            skLineSegment(sketch, "E907", {"start": v(11.31, 2.46) * mm, "end": v(11.38, 2.56) * mm});
            skLineSegment(sketch, "E908", {"start": v(11.38, 2.56) * mm, "end": v(11.46, 2.65) * mm});
            skLineSegment(sketch, "E909", {"start": v(11.46, 2.65) * mm, "end": v(11.57, 2.74) * mm});
            skLineSegment(sketch, "E910", {"start": v(11.57, 2.74) * mm, "end": v(11.65, 2.8) * mm});
            skLineSegment(sketch, "E911", {"start": v(11.65, 2.8) * mm, "end": v(11.66, 2.8) * mm});
            skLineSegment(sketch, "E912", {"start": v(11.66, 2.8) * mm, "end": v(11.68, 2.83) * mm});
            skLineSegment(sketch, "E913", {"start": v(11.68, 2.83) * mm, "end": v(11.7, 2.87) * mm});
            skLineSegment(sketch, "E914", {"start": v(11.7, 2.87) * mm, "end": v(11.74, 2.93) * mm});
            skLineSegment(sketch, "E915", {"start": v(11.74, 2.93) * mm, "end": v(11.78, 3) * mm});
            skLineSegment(sketch, "E916", {"start": v(11.78, 3) * mm, "end": v(11.82, 3.1) * mm});
            skLineSegment(sketch, "E917", {"start": v(11.82, 3.1) * mm, "end": v(11.86, 3.2) * mm});
            skLineSegment(sketch, "E918", {"start": v(11.86, 3.2) * mm, "end": v(11.9, 3.33) * mm});
            skLineSegment(sketch, "E919", {"start": v(11.9, 3.33) * mm, "end": v(11.93, 3.47) * mm});
            skLineSegment(sketch, "E920", {"start": v(11.93, 3.47) * mm, "end": v(11.96, 3.63) * mm});
            skLineSegment(sketch, "E921", {"start": v(11.96, 3.63) * mm, "end": v(11.98, 3.8) * mm});
            skLineSegment(sketch, "E922", {"start": v(11.98, 3.8) * mm, "end": v(11.98, 4) * mm});
            skLineSegment(sketch, "E923", {"start": v(11.98, 4) * mm, "end": v(11.98, 4.12) * mm});
            skLineSegment(sketch, "E924", {"start": v(11.98, 4.12) * mm, "end": v(11.82, 4.24) * mm});
            skLineSegment(sketch, "E925", {"start": v(11.82, 4.24) * mm, "end": v(11.66, 4.36) * mm});
            skLineSegment(sketch, "E926", {"start": v(11.66, 4.36) * mm, "end": v(11.54, 4.32) * mm});
            skLineSegment(sketch, "E927", {"start": v(11.54, 4.32) * mm, "end": v(11.36, 4.25) * mm});
            skLineSegment(sketch, "E928", {"start": v(11.36, 4.25) * mm, "end": v(11.2, 4.18) * mm});
            skLineSegment(sketch, "E929", {"start": v(11.2, 4.18) * mm, "end": v(11.05, 4.1) * mm});
            skLineSegment(sketch, "E930", {"start": v(11.05, 4.1) * mm, "end": v(10.93, 4.03) * mm});
            skLineSegment(sketch, "E931", {"start": v(10.93, 4.03) * mm, "end": v(10.82, 3.96) * mm});
            skLineSegment(sketch, "E932", {"start": v(10.82, 3.96) * mm, "end": v(10.73, 3.89) * mm});
            skLineSegment(sketch, "E933", {"start": v(10.73, 3.89) * mm, "end": v(10.66, 3.82) * mm});
            skLineSegment(sketch, "E934", {"start": v(10.66, 3.82) * mm, "end": v(10.6, 3.76) * mm});
            skLineSegment(sketch, "E935", {"start": v(10.6, 3.76) * mm, "end": v(10.56, 3.71) * mm});
            skLineSegment(sketch, "E936", {"start": v(10.56, 3.71) * mm, "end": v(10.53, 3.67) * mm});
            skLineSegment(sketch, "E937", {"start": v(10.53, 3.67) * mm, "end": v(10.5, 3.64) * mm});
            skLineSegment(sketch, "E938", {"start": v(10.5, 3.64) * mm, "end": v(10.5, 3.64) * mm});
            skLineSegment(sketch, "E939", {"start": v(10.5, 3.64) * mm, "end": v(10.48, 3.54) * mm});
            skLineSegment(sketch, "E940", {"start": v(10.48, 3.54) * mm, "end": v(10.42, 3.4) * mm});
            skLineSegment(sketch, "E941", {"start": v(10.42, 3.4) * mm, "end": v(10.36, 3.3) * mm});
            skLineSegment(sketch, "E942", {"start": v(10.36, 3.3) * mm, "end": v(10.29, 3.2) * mm});
            skLineSegment(sketch, "E943", {"start": v(10.29, 3.2) * mm, "end": v(10.21, 3.14) * mm});
            skLineSegment(sketch, "E944", {"start": v(10.21, 3.14) * mm, "end": v(10.14, 3.09) * mm});
            skLineSegment(sketch, "E945", {"start": v(10.14, 3.09) * mm, "end": v(10.06, 3.06) * mm});
            skLineSegment(sketch, "E946", {"start": v(10.06, 3.06) * mm, "end": v(10, 3.06) * mm});
            skLineSegment(sketch, "E947", {"start": v(10, 3.06) * mm, "end": v(9.92, 3.08) * mm});
            skLineSegment(sketch, "E948", {"start": v(9.92, 3.08) * mm, "end": v(9.86, 3.1) * mm});
            skLineSegment(sketch, "E949", {"start": v(9.86, 3.1) * mm, "end": v(9.66, 3.17) * mm});
            skLineSegment(sketch, "E950", {"start": v(9.66, 3.17) * mm, "end": v(9.59, 3.18) * mm});
            skLineSegment(sketch, "E951", {"start": v(9.59, 3.18) * mm, "end": v(9.53, 3.2) * mm});
            skLineSegment(sketch, "E952", {"start": v(9.53, 3.2) * mm, "end": v(9.47, 3.26) * mm});
            skLineSegment(sketch, "E953", {"start": v(9.47, 3.26) * mm, "end": v(9.43, 3.32) * mm});
            skLineSegment(sketch, "E954", {"start": v(9.43, 3.32) * mm, "end": v(9.4, 3.4) * mm});
            skLineSegment(sketch, "E955", {"start": v(9.4, 3.4) * mm, "end": v(9.37, 3.5) * mm});
            skLineSegment(sketch, "E956", {"start": v(9.37, 3.5) * mm, "end": v(9.37, 3.62) * mm});
            skLineSegment(sketch, "E957", {"start": v(9.37, 3.62) * mm, "end": v(9.38, 3.75) * mm});
            skLineSegment(sketch, "E958", {"start": v(9.38, 3.75) * mm, "end": v(9.42, 3.89) * mm});
            skLineSegment(sketch, "E959", {"start": v(9.42, 3.89) * mm, "end": v(9.45, 3.98) * mm});
            skLineSegment(sketch, "E960", {"start": v(9.45, 3.98) * mm, "end": v(9.45, 3.99) * mm});
            skLineSegment(sketch, "E961", {"start": v(9.45, 3.99) * mm, "end": v(9.45, 4.02) * mm});
            skLineSegment(sketch, "E962", {"start": v(9.45, 4.02) * mm, "end": v(9.45, 4.07) * mm});
            skLineSegment(sketch, "E963", {"start": v(9.45, 4.07) * mm, "end": v(9.45, 4.14) * mm});
            skLineSegment(sketch, "E964", {"start": v(9.45, 4.14) * mm, "end": v(9.44, 4.22) * mm});
            skLineSegment(sketch, "E965", {"start": v(9.44, 4.22) * mm, "end": v(9.41, 4.31) * mm});
            skLineSegment(sketch, "E966", {"start": v(9.41, 4.31) * mm, "end": v(9.38, 4.42) * mm});
            skLineSegment(sketch, "E967", {"start": v(9.38, 4.42) * mm, "end": v(9.34, 4.55) * mm});
            skLineSegment(sketch, "E968", {"start": v(9.34, 4.55) * mm, "end": v(9.28, 4.68) * mm});
            skLineSegment(sketch, "E969", {"start": v(9.28, 4.68) * mm, "end": v(9.21, 4.83) * mm});
            skLineSegment(sketch, "E970", {"start": v(9.21, 4.83) * mm, "end": v(9.12, 4.98) * mm});
            skLineSegment(sketch, "E971", {"start": v(9.12, 4.98) * mm, "end": v(9.01, 5.14) * mm});
            skLineSegment(sketch, "E972", {"start": v(9.01, 5.14) * mm, "end": v(8.94, 5.24) * mm});
            skLineSegment(sketch, "E973", {"start": v(8.94, 5.24) * mm, "end": v(8.74, 5.24) * mm});
            skLineSegment(sketch, "E974", {"start": v(8.74, 5.24) * mm, "end": v(8.54, 5.24) * mm});
            skLineSegment(sketch, "E975", {"start": v(8.54, 5.24) * mm, "end": v(8.47, 5.14) * mm});
            skLineSegment(sketch, "E976", {"start": v(8.47, 5.14) * mm, "end": v(8.36, 4.98) * mm});
            skLineSegment(sketch, "E977", {"start": v(8.36, 4.98) * mm, "end": v(8.27, 4.83) * mm});
            skLineSegment(sketch, "E978", {"start": v(8.27, 4.83) * mm, "end": v(8.2, 4.68) * mm});
            skLineSegment(sketch, "E979", {"start": v(8.2, 4.68) * mm, "end": v(8.14, 4.55) * mm});
            skLineSegment(sketch, "E980", {"start": v(8.14, 4.55) * mm, "end": v(8.1, 4.42) * mm});
            skLineSegment(sketch, "E981", {"start": v(8.1, 4.42) * mm, "end": v(8.07, 4.31) * mm});
            skLineSegment(sketch, "E982", {"start": v(8.07, 4.31) * mm, "end": v(8.04, 4.22) * mm});
            skLineSegment(sketch, "E983", {"start": v(8.04, 4.22) * mm, "end": v(8.03, 4.14) * mm});
            skLineSegment(sketch, "E984", {"start": v(8.03, 4.14) * mm, "end": v(8.03, 4.07) * mm});
            skLineSegment(sketch, "E985", {"start": v(8.03, 4.07) * mm, "end": v(8.03, 4.02) * mm});
            skLineSegment(sketch, "E986", {"start": v(8.03, 4.02) * mm, "end": v(8.03, 3.99) * mm});
            skLineSegment(sketch, "E987", {"start": v(8.03, 3.99) * mm, "end": v(8.03, 3.98) * mm});
            skLineSegment(sketch, "E988", {"start": v(8.03, 3.98) * mm, "end": v(8.06, 3.89) * mm});
            skLineSegment(sketch, "E989", {"start": v(8.06, 3.89) * mm, "end": v(8.1, 3.75) * mm});
            skLineSegment(sketch, "E990", {"start": v(8.1, 3.75) * mm, "end": v(8.11, 3.62) * mm});
            skLineSegment(sketch, "E991", {"start": v(8.11, 3.62) * mm, "end": v(8.1, 3.5) * mm});
            skLineSegment(sketch, "E992", {"start": v(8.1, 3.5) * mm, "end": v(8.09, 3.4) * mm});
            skLineSegment(sketch, "E993", {"start": v(8.09, 3.4) * mm, "end": v(8.05, 3.32) * mm});
            skLineSegment(sketch, "E994", {"start": v(8.05, 3.32) * mm, "end": v(8, 3.26) * mm});
            skLineSegment(sketch, "E995", {"start": v(8, 3.26) * mm, "end": v(7.95, 3.2) * mm});
            skLineSegment(sketch, "E996", {"start": v(7.95, 3.2) * mm, "end": v(7.9, 3.18) * mm});
            skLineSegment(sketch, "E997", {"start": v(7.9, 3.18) * mm, "end": v(7.82, 3.17) * mm});
            skLineSegment(sketch, "E998", {"start": v(7.82, 3.17) * mm, "end": v(7.62, 3.1) * mm});
            skLineSegment(sketch, "E999", {"start": v(7.62, 3.1) * mm, "end": v(7.56, 3.08) * mm});
            skLineSegment(sketch, "E1000", {"start": v(7.56, 3.08) * mm, "end": v(7.49, 3.06) * mm});
            skLineSegment(sketch, "E1001", {"start": v(7.49, 3.06) * mm, "end": v(7.42, 3.06) * mm});
            skLineSegment(sketch, "E1002", {"start": v(7.42, 3.06) * mm, "end": v(7.34, 3.09) * mm});
            skLineSegment(sketch, "E1003", {"start": v(7.34, 3.09) * mm, "end": v(7.27, 3.14) * mm});
            skLineSegment(sketch, "E1004", {"start": v(7.27, 3.14) * mm, "end": v(7.2, 3.2) * mm});
            skLineSegment(sketch, "E1005", {"start": v(7.2, 3.2) * mm, "end": v(7.12, 3.3) * mm});
            skLineSegment(sketch, "E1006", {"start": v(7.12, 3.3) * mm, "end": v(7.06, 3.4) * mm});
            skLineSegment(sketch, "E1007", {"start": v(7.06, 3.4) * mm, "end": v(7, 3.54) * mm});
            skLineSegment(sketch, "E1008", {"start": v(7, 3.54) * mm, "end": v(6.98, 3.64) * mm});
            skLineSegment(sketch, "E1009", {"start": v(6.98, 3.64) * mm, "end": v(6.97, 3.64) * mm});
            skLineSegment(sketch, "E1010", {"start": v(6.97, 3.64) * mm, "end": v(6.95, 3.67) * mm});
            skLineSegment(sketch, "E1011", {"start": v(6.95, 3.67) * mm, "end": v(6.92, 3.71) * mm});
            skLineSegment(sketch, "E1012", {"start": v(6.92, 3.71) * mm, "end": v(6.88, 3.76) * mm});
            skLineSegment(sketch, "E1013", {"start": v(6.88, 3.76) * mm, "end": v(6.82, 3.82) * mm});
            skLineSegment(sketch, "E1014", {"start": v(6.82, 3.82) * mm, "end": v(6.75, 3.89) * mm});
            skLineSegment(sketch, "E1015", {"start": v(6.75, 3.89) * mm, "end": v(6.66, 3.96) * mm});
            skLineSegment(sketch, "E1016", {"start": v(6.66, 3.96) * mm, "end": v(6.55, 4.03) * mm});
            skLineSegment(sketch, "E1017", {"start": v(6.55, 4.03) * mm, "end": v(6.43, 4.1) * mm});
            skLineSegment(sketch, "E1018", {"start": v(6.43, 4.1) * mm, "end": v(6.28, 4.18) * mm});
            skLineSegment(sketch, "E1019", {"start": v(6.28, 4.18) * mm, "end": v(6.12, 4.25) * mm});
            skLineSegment(sketch, "E1020", {"start": v(6.12, 4.25) * mm, "end": v(5.94, 4.32) * mm});
            skLineSegment(sketch, "E1021", {"start": v(5.94, 4.32) * mm, "end": v(5.82, 4.36) * mm});
            skLineSegment(sketch, "E1022", {"start": v(5.82, 4.36) * mm, "end": v(5.66, 4.24) * mm});
            skLineSegment(sketch, "E1023", {"start": v(5.66, 4.24) * mm, "end": v(5.5, 4.12) * mm});
            skLineSegment(sketch, "E1024", {"start": v(5.5, 4.12) * mm, "end": v(5.5, 4) * mm});
            skLineSegment(sketch, "E1025", {"start": v(5.5, 4) * mm, "end": v(5.5, 3.8) * mm});
            skLineSegment(sketch, "E1026", {"start": v(5.5, 3.8) * mm, "end": v(5.52, 3.63) * mm});
            skLineSegment(sketch, "E1027", {"start": v(5.52, 3.63) * mm, "end": v(5.55, 3.47) * mm});
            skLineSegment(sketch, "E1028", {"start": v(5.55, 3.47) * mm, "end": v(5.58, 3.33) * mm});
            skLineSegment(sketch, "E1029", {"start": v(5.58, 3.33) * mm, "end": v(5.62, 3.2) * mm});
            skLineSegment(sketch, "E1030", {"start": v(5.62, 3.2) * mm, "end": v(5.66, 3.1) * mm});
            skLineSegment(sketch, "E1031", {"start": v(5.66, 3.1) * mm, "end": v(5.7, 3) * mm});
            skLineSegment(sketch, "E1032", {"start": v(5.7, 3) * mm, "end": v(5.74, 2.93) * mm});
            skLineSegment(sketch, "E1033", {"start": v(5.74, 2.93) * mm, "end": v(5.77, 2.87) * mm});
            skLineSegment(sketch, "E1034", {"start": v(5.77, 2.87) * mm, "end": v(5.8, 2.83) * mm});
            skLineSegment(sketch, "E1035", {"start": v(5.8, 2.83) * mm, "end": v(5.82, 2.8) * mm});
            skLineSegment(sketch, "E1036", {"start": v(5.82, 2.8) * mm, "end": v(5.83, 2.8) * mm});
            skLineSegment(sketch, "E1037", {"start": v(5.83, 2.8) * mm, "end": v(5.9, 2.74) * mm});
            skLineSegment(sketch, "E1038", {"start": v(5.9, 2.74) * mm, "end": v(6.02, 2.65) * mm});
            skLineSegment(sketch, "E1039", {"start": v(6.02, 2.65) * mm, "end": v(6.1, 2.56) * mm});
            skLineSegment(sketch, "E1040", {"start": v(6.1, 2.56) * mm, "end": v(6.17, 2.46) * mm});
            skLineSegment(sketch, "E1041", {"start": v(6.17, 2.46) * mm, "end": v(6.21, 2.37) * mm});
            skLineSegment(sketch, "E1042", {"start": v(6.21, 2.37) * mm, "end": v(6.23, 2.28) * mm});
            skLineSegment(sketch, "E1043", {"start": v(6.23, 2.28) * mm, "end": v(6.23, 2.2) * mm});
            skLineSegment(sketch, "E1044", {"start": v(6.23, 2.2) * mm, "end": v(6.22, 2.13) * mm});
            skLineSegment(sketch, "E1045", {"start": v(6.22, 2.13) * mm, "end": v(6.18, 2.08) * mm});
            skLineSegment(sketch, "E1046", {"start": v(6.18, 2.08) * mm, "end": v(6.13, 2.02) * mm});
            skLineSegment(sketch, "E1047", {"start": v(6.13, 2.02) * mm, "end": v(6.01, 1.85) * mm});
            skLineSegment(sketch, "E1048", {"start": v(6.01, 1.85) * mm, "end": v(5.97, 1.8) * mm});
            skLineSegment(sketch, "E1049", {"start": v(5.97, 1.8) * mm, "end": v(5.93, 1.74) * mm});
            skLineSegment(sketch, "E1050", {"start": v(5.93, 1.74) * mm, "end": v(5.87, 1.7) * mm});
            skLineSegment(sketch, "E1051", {"start": v(5.87, 1.7) * mm, "end": v(5.8, 1.68) * mm});
            skLineSegment(sketch, "E1052", {"start": v(5.8, 1.68) * mm, "end": v(5.7, 1.67) * mm});
            skLineSegment(sketch, "E1053", {"start": v(5.7, 1.67) * mm, "end": v(5.6, 1.68) * mm});
            skLineSegment(sketch, "E1054", {"start": v(5.6, 1.68) * mm, "end": v(5.5, 1.72) * mm});
            skLineSegment(sketch, "E1055", {"start": v(5.5, 1.72) * mm, "end": v(5.38, 1.77) * mm});
            skLineSegment(sketch, "E1056", {"start": v(5.38, 1.77) * mm, "end": v(5.25, 1.85) * mm});
            skLineSegment(sketch, "E1057", {"start": v(5.25, 1.85) * mm, "end": v(5.18, 1.9) * mm});
            skLineSegment(sketch, "E1058", {"start": v(5.18, 1.9) * mm, "end": v(5.17, 1.9) * mm});
            skLineSegment(sketch, "E1059", {"start": v(5.17, 1.9) * mm, "end": v(5.14, 1.92) * mm});
            skLineSegment(sketch, "E1060", {"start": v(5.14, 1.92) * mm, "end": v(5.09, 1.94) * mm});
            skLineSegment(sketch, "E1061", {"start": v(5.09, 1.94) * mm, "end": v(5.02, 1.95) * mm});
            skLineSegment(sketch, "E1062", {"start": v(5.02, 1.95) * mm, "end": v(4.94, 1.96) * mm});
            skLineSegment(sketch, "E1063", {"start": v(4.94, 1.96) * mm, "end": v(4.84, 1.97) * mm});
            skLineSegment(sketch, "E1064", {"start": v(4.84, 1.97) * mm, "end": v(4.73, 1.98) * mm});
            skLineSegment(sketch, "E1065", {"start": v(4.73, 1.98) * mm, "end": v(4.6, 1.98) * mm});
            skLineSegment(sketch, "E1066", {"start": v(4.6, 1.98) * mm, "end": v(4.46, 1.96) * mm});
            skLineSegment(sketch, "E1067", {"start": v(4.46, 1.96) * mm, "end": v(4.3, 1.94) * mm});
            skLineSegment(sketch, "E1068", {"start": v(4.3, 1.94) * mm, "end": v(4.12, 1.9) * mm});
            skLineSegment(sketch, "E1069", {"start": v(4.12, 1.9) * mm, "end": v(3.93, 1.85) * mm});
            skLineSegment(sketch, "E1070", {"start": v(3.93, 1.85) * mm, "end": v(3.82, 1.81) * mm});
            skLineSegment(sketch, "E1071", {"start": v(8.27, 1.16) * mm, "end": v(8.35, 1.19) * mm});
            skLineSegment(sketch, "E1072", {"start": v(8.35, 1.19) * mm, "end": v(8.44, 1.21) * mm});
            skLineSegment(sketch, "E1073", {"start": v(8.44, 1.21) * mm, "end": v(8.52, 1.23) * mm});
            skLineSegment(sketch, "E1074", {"start": v(8.52, 1.23) * mm, "end": v(8.6, 1.24) * mm});
            skLineSegment(sketch, "E1075", {"start": v(8.6, 1.24) * mm, "end": v(8.7, 1.25) * mm});
            skLineSegment(sketch, "E1076", {"start": v(8.7, 1.25) * mm, "end": v(8.78, 1.25) * mm});
            skLineSegment(sketch, "E1077", {"start": v(8.78, 1.25) * mm, "end": v(8.87, 1.24) * mm});
            skLineSegment(sketch, "E1078", {"start": v(8.87, 1.24) * mm, "end": v(8.96, 1.23) * mm});
            skLineSegment(sketch, "E1079", {"start": v(8.96, 1.23) * mm, "end": v(9.04, 1.21) * mm});
            skLineSegment(sketch, "E1080", {"start": v(9.04, 1.21) * mm, "end": v(9.13, 1.19) * mm});
            skLineSegment(sketch, "E1081", {"start": v(9.13, 1.19) * mm, "end": v(9.2, 1.16) * mm});
            skLineSegment(sketch, "E1082", {"start": v(9.2, 1.16) * mm, "end": v(9.29, 1.12) * mm});
            skLineSegment(sketch, "E1083", {"start": v(9.29, 1.12) * mm, "end": v(9.37, 1.08) * mm});
            skLineSegment(sketch, "E1084", {"start": v(9.37, 1.08) * mm, "end": v(9.44, 1.04) * mm});
            skLineSegment(sketch, "E1085", {"start": v(9.44, 1.04) * mm, "end": v(9.5, 0.99) * mm});
            skLineSegment(sketch, "E1086", {"start": v(9.5, 0.99) * mm, "end": v(9.58, 0.93) * mm});
            skLineSegment(sketch, "E1087", {"start": v(9.58, 0.93) * mm, "end": v(9.64, 0.87) * mm});
            skLineSegment(sketch, "E1088", {"start": v(9.64, 0.87) * mm, "end": v(9.7, 0.8) * mm});
            skLineSegment(sketch, "E1089", {"start": v(9.7, 0.8) * mm, "end": v(9.75, 0.73) * mm});
            skLineSegment(sketch, "E1090", {"start": v(9.75, 0.73) * mm, "end": v(9.8, 0.66) * mm});
            skLineSegment(sketch, "E1091", {"start": v(9.8, 0.66) * mm, "end": v(9.84, 0.59) * mm});
            skLineSegment(sketch, "E1092", {"start": v(9.84, 0.59) * mm, "end": v(9.88, 0.5) * mm});
            skLineSegment(sketch, "E1093", {"start": v(9.88, 0.5) * mm, "end": v(9.91, 0.43) * mm});
            skLineSegment(sketch, "E1094", {"start": v(9.91, 0.43) * mm, "end": v(9.94, 0.34) * mm});
            skLineSegment(sketch, "E1095", {"start": v(9.94, 0.34) * mm, "end": v(9.96, 0.26) * mm});
            skLineSegment(sketch, "E1096", {"start": v(9.96, 0.26) * mm, "end": v(9.98, 0.17) * mm});
            skLineSegment(sketch, "E1097", {"start": v(9.98, 0.17) * mm, "end": v(9.99, 0.09) * mm});
            skLineSegment(sketch, "E1098", {"start": v(9.99, 0.09) * mm, "end": v(10, 0) * mm});
            skLineSegment(sketch, "E1099", {"start": v(10, 0) * mm, "end": v(9.99, -0.09) * mm});
            skLineSegment(sketch, "E1100", {"start": v(9.99, -0.09) * mm, "end": v(9.98, -0.17) * mm});
            skLineSegment(sketch, "E1101", {"start": v(9.98, -0.17) * mm, "end": v(9.96, -0.26) * mm});
            skLineSegment(sketch, "E1102", {"start": v(9.96, -0.26) * mm, "end": v(9.94, -0.34) * mm});
            skLineSegment(sketch, "E1103", {"start": v(9.94, -0.34) * mm, "end": v(9.91, -0.43) * mm});
            skLineSegment(sketch, "E1104", {"start": v(9.91, -0.43) * mm, "end": v(9.88, -0.5) * mm});
            skLineSegment(sketch, "E1105", {"start": v(9.88, -0.5) * mm, "end": v(9.84, -0.59) * mm});
            skLineSegment(sketch, "E1106", {"start": v(9.84, -0.59) * mm, "end": v(9.8, -0.66) * mm});
            skLineSegment(sketch, "E1107", {"start": v(9.8, -0.66) * mm, "end": v(9.75, -0.73) * mm});
            skLineSegment(sketch, "E1108", {"start": v(9.75, -0.73) * mm, "end": v(9.7, -0.8) * mm});
            skLineSegment(sketch, "E1109", {"start": v(9.7, -0.8) * mm, "end": v(9.64, -0.87) * mm});
            skLineSegment(sketch, "E1110", {"start": v(9.64, -0.87) * mm, "end": v(9.58, -0.93) * mm});
            skLineSegment(sketch, "E1111", {"start": v(9.58, -0.93) * mm, "end": v(9.5, -0.99) * mm});
            skLineSegment(sketch, "E1112", {"start": v(9.5, -0.99) * mm, "end": v(9.44, -1.04) * mm});
            skLineSegment(sketch, "E1113", {"start": v(9.44, -1.04) * mm, "end": v(9.37, -1.08) * mm});
            skLineSegment(sketch, "E1114", {"start": v(9.37, -1.08) * mm, "end": v(9.29, -1.12) * mm});
            skLineSegment(sketch, "E1115", {"start": v(9.29, -1.12) * mm, "end": v(9.2, -1.16) * mm});
            skLineSegment(sketch, "E1116", {"start": v(9.2, -1.16) * mm, "end": v(9.13, -1.19) * mm});
            skLineSegment(sketch, "E1117", {"start": v(9.13, -1.19) * mm, "end": v(9.04, -1.21) * mm});
            skLineSegment(sketch, "E1118", {"start": v(9.04, -1.21) * mm, "end": v(8.96, -1.23) * mm});
            skLineSegment(sketch, "E1119", {"start": v(8.96, -1.23) * mm, "end": v(8.87, -1.24) * mm});
            skLineSegment(sketch, "E1120", {"start": v(8.87, -1.24) * mm, "end": v(8.78, -1.25) * mm});
            skLineSegment(sketch, "E1121", {"start": v(8.78, -1.25) * mm, "end": v(8.7, -1.25) * mm});
            skLineSegment(sketch, "E1122", {"start": v(8.7, -1.25) * mm, "end": v(8.6, -1.24) * mm});
            skLineSegment(sketch, "E1123", {"start": v(8.6, -1.24) * mm, "end": v(8.52, -1.23) * mm});
            skLineSegment(sketch, "E1124", {"start": v(8.52, -1.23) * mm, "end": v(8.44, -1.21) * mm});
            skLineSegment(sketch, "E1125", {"start": v(8.44, -1.21) * mm, "end": v(8.35, -1.19) * mm});
            skLineSegment(sketch, "E1126", {"start": v(8.35, -1.19) * mm, "end": v(8.27, -1.16) * mm});
            skLineSegment(sketch, "E1127", {"start": v(8.27, -1.16) * mm, "end": v(8.2, -1.12) * mm});
            skLineSegment(sketch, "E1128", {"start": v(8.2, -1.12) * mm, "end": v(8.12, -1.08) * mm});
            skLineSegment(sketch, "E1129", {"start": v(8.12, -1.08) * mm, "end": v(8.04, -1.04) * mm});
            skLineSegment(sketch, "E1130", {"start": v(8.04, -1.04) * mm, "end": v(7.97, -0.99) * mm});
            skLineSegment(sketch, "E1131", {"start": v(7.97, -0.99) * mm, "end": v(7.9, -0.93) * mm});
            skLineSegment(sketch, "E1132", {"start": v(7.9, -0.93) * mm, "end": v(7.84, -0.87) * mm});
            skLineSegment(sketch, "E1133", {"start": v(7.84, -0.87) * mm, "end": v(7.78, -0.8) * mm});
            skLineSegment(sketch, "E1134", {"start": v(7.78, -0.8) * mm, "end": v(7.73, -0.73) * mm});
            skLineSegment(sketch, "E1135", {"start": v(7.73, -0.73) * mm, "end": v(7.68, -0.66) * mm});
            skLineSegment(sketch, "E1136", {"start": v(7.68, -0.66) * mm, "end": v(7.64, -0.59) * mm});
            skLineSegment(sketch, "E1137", {"start": v(7.64, -0.59) * mm, "end": v(7.6, -0.5) * mm});
            skLineSegment(sketch, "E1138", {"start": v(7.6, -0.5) * mm, "end": v(7.57, -0.43) * mm});
            skLineSegment(sketch, "E1139", {"start": v(7.57, -0.43) * mm, "end": v(7.54, -0.34) * mm});
            skLineSegment(sketch, "E1140", {"start": v(7.54, -0.34) * mm, "end": v(7.52, -0.26) * mm});
            skLineSegment(sketch, "E1141", {"start": v(7.52, -0.26) * mm, "end": v(7.5, -0.17) * mm});
            skLineSegment(sketch, "E1142", {"start": v(7.5, -0.17) * mm, "end": v(7.5, -0.09) * mm});
            skLineSegment(sketch, "E1143", {"start": v(7.5, -0.09) * mm, "end": v(7.5, 0) * mm});
            skLineSegment(sketch, "E1144", {"start": v(7.5, 0) * mm, "end": v(7.5, 0.09) * mm});
            skLineSegment(sketch, "E1145", {"start": v(7.5, 0.09) * mm, "end": v(7.5, 0.17) * mm});
            skLineSegment(sketch, "E1146", {"start": v(7.5, 0.17) * mm, "end": v(7.52, 0.26) * mm});
            skLineSegment(sketch, "E1147", {"start": v(7.52, 0.26) * mm, "end": v(7.54, 0.34) * mm});
            skLineSegment(sketch, "E1148", {"start": v(7.54, 0.34) * mm, "end": v(7.57, 0.43) * mm});
            skLineSegment(sketch, "E1149", {"start": v(7.57, 0.43) * mm, "end": v(7.6, 0.5) * mm});
            skLineSegment(sketch, "E1150", {"start": v(7.6, 0.5) * mm, "end": v(7.64, 0.59) * mm});
            skLineSegment(sketch, "E1151", {"start": v(7.64, 0.59) * mm, "end": v(7.68, 0.66) * mm});
            skLineSegment(sketch, "E1152", {"start": v(7.68, 0.66) * mm, "end": v(7.73, 0.73) * mm});
            skLineSegment(sketch, "E1153", {"start": v(7.73, 0.73) * mm, "end": v(7.78, 0.8) * mm});
            skLineSegment(sketch, "E1154", {"start": v(7.78, 0.8) * mm, "end": v(7.84, 0.87) * mm});
            skLineSegment(sketch, "E1155", {"start": v(7.84, 0.87) * mm, "end": v(7.9, 0.93) * mm});
            skLineSegment(sketch, "E1156", {"start": v(7.9, 0.93) * mm, "end": v(7.97, 0.99) * mm});
            skLineSegment(sketch, "E1157", {"start": v(7.97, 0.99) * mm, "end": v(8.04, 1.04) * mm});
            skLineSegment(sketch, "E1158", {"start": v(8.04, 1.04) * mm, "end": v(8.12, 1.08) * mm});
            skLineSegment(sketch, "E1159", {"start": v(8.12, 1.08) * mm, "end": v(8.2, 1.12) * mm});
            skLineSegment(sketch, "E1160", {"start": v(8.2, 1.12) * mm, "end": v(8.27, 1.16) * mm});
            skCircle(sketch, "E1161.0", {"center": v(0, 0) * mm, "radius": 1.5 * mm});
            skSolve(sketch);
        }
        {
            var Q0;
            Q0=makeQuery(id+"F1.imprint","IMPRINT",FACE,{"disambiguationData":[TD([[makeQuery(id+"F1.imprint","IMPRINT",EDGE,{"derivedFrom":sQuery(id+"F1.wireOp",EDGE,"E1")}),1.0]])]});
            extrude(context, id + "F2", {"entities" : qUnion([Q0]), "depth" : 3 * mm});
        }
    });
